# Revit family: LL-Double Angle
name_source: partatom
category: Structural Framing
revit_build: Autodesk Revit Architecture 2012 (Build: 20110210_1515)
units: mm (PartAtom-declared; Revit-internal decimal feet)

## types (597) — shared parameters
Assembly Code = B10

## per-type parameters (varying)
| type | A | Legs | Space | W | b | d | t | y |
| 2L8X8X1-1/8 | 33.6 in² | Equal | 0' - 0" | 114 | 0' - 8" | 0' - 8" | 0' - 1 1/8" | 0' - 2 3/8" |
| 2L8X8X1-1/8X3/8 | 33.6 in² | Equal | 0' - 0 3/8" | 114 | 0' - 8" | 0' - 8" | 0' - 1 1/8" | 0' - 2 3/8" |
| 2L8X8X1-1/8X3/4 | 33.6 in² | Equal | 0' - 0 3/4" | 114 | 0' - 8" | 0' - 8" | 0' - 1 1/8" | 0' - 2 3/8" |
| 2L8X8X1 | 30.2 in² | Equal | 0' - 0" | 103 | 0' - 8" | 0' - 8" | 0' - 1" | 0' - 2 3/8" |
| 2L8X8X1X3/8 | 30.2 in² | Equal | 0' - 0 3/8" | 103 | 0' - 8" | 0' - 8" | 0' - 1" | 0' - 2 3/8" |
| 2L8X8X1X3/4 | 30.2 in² | Equal | 0' - 0 3/4" | 103 | 0' - 8" | 0' - 8" | 0' - 1" | 0' - 2 3/8" |
| 2L8X8X7/8 | 26.6 in² | Equal | 0' - 0" | 90.6 | 0' - 8" | 0' - 8" | 0' - 0 7/8" | 0' - 2 5/16" |
| 2L8X8X7/8X3/8 | 26.6 in² | Equal | 0' - 0 3/8" | 90.6 | 0' - 8" | 0' - 8" | 0' - 0 7/8" | 0' - 2 5/16" |
| 2L8X8X7/8X3/4 | 26.6 in² | Equal | 0' - 0 3/4" | 90.6 | 0' - 8" | 0' - 8" | 0' - 0 7/8" | 0' - 2 5/16" |
| 2L8X8X3/4 | 23 in² | Equal | 0' - 0" | 78.4 | 0' - 8" | 0' - 8" | 0' - 0 3/4" | 0' - 2 1/4" |
| 2L8X8X3/4X3/8 | 23 in² | Equal | 0' - 0 3/8" | 78.4 | 0' - 8" | 0' - 8" | 0' - 0 3/4" | 0' - 2 1/4" |
| 2L8X8X3/4X3/4 | 23 in² | Equal | 0' - 0 3/4" | 78.4 | 0' - 8" | 0' - 8" | 0' - 0 3/4" | 0' - 2 1/4" |
| 2L8X8X5/8 | 19.4 in² | Equal | 0' - 0" | 66 | 0' - 8" | 0' - 8" | 0' - 0 5/8" | 0' - 2 3/16" |
| 2L8X8X5/8X3/8 | 19.4 in² | Equal | 0' - 0 3/8" | 66 | 0' - 8" | 0' - 8" | 0' - 0 5/8" | 0' - 2 3/16" |
| 2L8X8X5/8X3/4 | 19.4 in² | Equal | 0' - 0 3/4" | 66 | 0' - 8" | 0' - 8" | 0' - 0 5/8" | 0' - 2 3/16" |
| 2L8X8X9/16 | 17.5 in² | Equal | 0' - 0" | 59.7 | 0' - 8" | 0' - 8" | 0' - 0 9/16" | 0' - 2 3/16" |
| 2L8X8X9/16X3/8 | 17.5 in² | Equal | 0' - 0 3/8" | 59.7 | 0' - 8" | 0' - 8" | 0' - 0 9/16" | 0' - 2 3/16" |
| 2L8X8X9/16X3/4 | 17.5 in² | Equal | 0' - 0 3/4" | 59.7 | 0' - 8" | 0' - 8" | 0' - 0 9/16" | 0' - 2 3/16" |
| 2L8X8X1/2 | 15.7 in² | Equal | 0' - 0" | 53.3 | 0' - 8" | 0' - 8" | 0' - 0 1/2" | 0' - 2 3/16" |
| 2L8X8X1/2X3/8 | 15.7 in² | Equal | 0' - 0 3/8" | 53.3 | 0' - 8" | 0' - 8" | 0' - 0 1/2" | 0' - 2 3/16" |
| 2L8X8X1/2X3/4 | 15.7 in² | Equal | 0' - 0 3/4" | 53.3 | 0' - 8" | 0' - 8" | 0' - 0 1/2" | 0' - 2 3/16" |
| 2L6X6X1 | 22 in² | Equal | 0' - 0" | 75 | 0' - 6" | 0' - 6" | 0' - 1" | 0' - 1 7/8" |
| 2L6X6X1X3/8 | 22 in² | Equal | 0' - 0 3/8" | 75 | 0' - 6" | 0' - 6" | 0' - 1" | 0' - 1 7/8" |
| 2L6X6X1X3/4 | 22 in² | Equal | 0' - 0 3/4" | 75 | 0' - 6" | 0' - 6" | 0' - 1" | 0' - 1 7/8" |
| 2L6X6X7/8 | 19.5 in² | Equal | 0' - 0" | 66.4 | 0' - 6" | 0' - 6" | 0' - 0 7/8" | 0' - 1 13/16" |
| 2L6X6X7/8X3/8 | 19.5 in² | Equal | 0' - 0 3/8" | 66.4 | 0' - 6" | 0' - 6" | 0' - 0 7/8" | 0' - 1 13/16" |
| 2L6X6X7/8X3/4 | 19.5 in² | Equal | 0' - 0 3/4" | 66.4 | 0' - 6" | 0' - 6" | 0' - 0 7/8" | 0' - 1 13/16" |
| 2L6X6X3/4 | 16.9 in² | Equal | 0' - 0" | 57.6 | 0' - 6" | 0' - 6" | 0' - 0 3/4" | 0' - 1 3/4" |
| 2L6X6X3/4X3/8 | 16.9 in² | Equal | 0' - 0 3/8" | 57.6 | 0' - 6" | 0' - 6" | 0' - 0 3/4" | 0' - 1 3/4" |
| 2L6X6X3/4X3/4 | 16.9 in² | Equal | 0' - 0 3/4" | 57.6 | 0' - 6" | 0' - 6" | 0' - 0 3/4" | 0' - 1 3/4" |
| 2L6X6X5/8 | 14.3 in² | Equal | 0' - 0" | 48.5 | 0' - 6" | 0' - 6" | 0' - 0 5/8" | 0' - 1 3/4" |
| 2L6X6X5/8X3/8 | 14.3 in² | Equal | 0' - 0 3/8" | 48.5 | 0' - 6" | 0' - 6" | 0' - 0 5/8" | 0' - 1 3/4" |
| 2L6X6X5/8X3/4 | 14.3 in² | Equal | 0' - 0 3/4" | 48.5 | 0' - 6" | 0' - 6" | 0' - 0 5/8" | 0' - 1 3/4" |
| 2L6X6X9/16 | 12.9 in² | Equal | 0' - 0" | 43.9 | 0' - 6" | 0' - 6" | 0' - 0 9/16" | 0' - 1 11/16" |
| 2L6X6X9/16X3/8 | 12.9 in² | Equal | 0' - 0 3/8" | 43.9 | 0' - 6" | 0' - 6" | 0' - 0 9/16" | 0' - 1 11/16" |
| 2L6X6X9/16X3/4 | 12.9 in² | Equal | 0' - 0 3/4" | 43.9 | 0' - 6" | 0' - 6" | 0' - 0 9/16" | 0' - 1 11/16" |
| 2L6X6X1/2 | 11.5 in² | Equal | 0' - 0" | 39.3 | 0' - 6" | 0' - 6" | 0' - 0 1/2" | 0' - 1 11/16" |
| 2L6X6X1/2X3/8 | 11.5 in² | Equal | 0' - 0 3/8" | 39.3 | 0' - 6" | 0' - 6" | 0' - 0 1/2" | 0' - 1 11/16" |
| 2L6X6X1/2X3/4 | 11.5 in² | Equal | 0' - 0 3/4" | 39.3 | 0' - 6" | 0' - 6" | 0' - 0 1/2" | 0' - 1 11/16" |
| 2L6X6X7/16 | 10.2 in² | Equal | 0' - 0" | 34.6 | 0' - 6" | 0' - 6" | 0' - 0 7/16" | 0' - 1 5/8" |
| 2L6X6X7/16X3/8 | 10.2 in² | Equal | 0' - 0 3/8" | 34.6 | 0' - 6" | 0' - 6" | 0' - 0 7/16" | 0' - 1 5/8" |
| 2L6X6X7/16X3/4 | 10.2 in² | Equal | 0' - 0 3/4" | 34.6 | 0' - 6" | 0' - 6" | 0' - 0 7/16" | 0' - 1 5/8" |
| 2L6X6X3/8 | 8.76 in² | Equal | 0' - 0" | 29.8 | 0' - 6" | 0' - 6" | 0' - 0 3/8" | 0' - 1 5/8" |
| 2L6X6X3/8X3/8 | 8.76 in² | Equal | 0' - 0 3/8" | 29.8 | 0' - 6" | 0' - 6" | 0' - 0 3/8" | 0' - 1 5/8" |
| 2L6X6X3/8X3/4 | 8.76 in² | Equal | 0' - 0 3/4" | 29.8 | 0' - 6" | 0' - 6" | 0' - 0 3/8" | 0' - 1 5/8" |
| 2L6X6X5/16 | 7.34 in² | Equal | 0' - 0" | 25 | 0' - 6" | 0' - 6" | 0' - 0 5/16" | 0' - 1 5/8" |
| 2L6X6X5/16X3/8 | 7.34 in² | Equal | 0' - 0 3/8" | 25 | 0' - 6" | 0' - 6" | 0' - 0 5/16" | 0' - 1 5/8" |
| 2L6X6X5/16X3/4 | 7.34 in² | Equal | 0' - 0 3/4" | 25 | 0' - 6" | 0' - 6" | 0' - 0 5/16" | 0' - 1 5/8" |
| 2L5X5X7/8 | 16 in² | Equal | 0' - 0" | 54.6 | 0' - 5" | 0' - 5" | 0' - 0 7/8" | 0' - 1 9/16" |
| 2L5X5X7/8X3/8 | 16 in² | Equal | 0' - 0 3/8" | 54.6 | 0' - 5" | 0' - 5" | 0' - 0 7/8" | 0' - 1 9/16" |
| 2L5X5X7/8X3/4 | 16 in² | Equal | 0' - 0 3/4" | 54.6 | 0' - 5" | 0' - 5" | 0' - 0 7/8" | 0' - 1 9/16" |
| 2L5X5X3/4 | 14 in² | Equal | 0' - 0" | 47.5 | 0' - 5" | 0' - 5" | 0' - 0 3/4" | 0' - 1 1/2" |
| 2L5X5X3/4X3/8 | 14 in² | Equal | 0' - 0 3/8" | 47.5 | 0' - 5" | 0' - 5" | 0' - 0 3/4" | 0' - 1 1/2" |
| 2L5X5X3/4X3/4 | 14 in² | Equal | 0' - 0 3/4" | 47.5 | 0' - 5" | 0' - 5" | 0' - 0 3/4" | 0' - 1 1/2" |
| 2L5X5X5/8 | 11.8 in² | Equal | 0' - 0" | 40.1 | 0' - 5" | 0' - 5" | 0' - 0 5/8" | 0' - 1 1/2" |
| 2L5X5X5/8X3/8 | 11.8 in² | Equal | 0' - 0 3/8" | 40.1 | 0' - 5" | 0' - 5" | 0' - 0 5/8" | 0' - 1 1/2" |
| 2L5X5X5/8X3/4 | 11.8 in² | Equal | 0' - 0 3/4" | 40.1 | 0' - 5" | 0' - 5" | 0' - 0 5/8" | 0' - 1 1/2" |
| 2L5X5X1/2 | 9.58 in² | Equal | 0' - 0" | 32.6 | 0' - 5" | 0' - 5" | 0' - 0 1/2" | 0' - 1 7/16" |
| 2L5X5X1/2X3/8 | 9.58 in² | Equal | 0' - 0 3/8" | 32.6 | 0' - 5" | 0' - 5" | 0' - 0 1/2" | 0' - 1 7/16" |
| 2L5X5X1/2X3/4 | 9.58 in² | Equal | 0' - 0 3/4" | 32.6 | 0' - 5" | 0' - 5" | 0' - 0 1/2" | 0' - 1 7/16" |
| 2L5X5X7/16 | 8.44 in² | Equal | 0' - 0" | 28.7 | 0' - 5" | 0' - 5" | 0' - 0 7/16" | 0' - 1 3/8" |
| 2L5X5X7/16X3/8 | 8.44 in² | Equal | 0' - 0 3/8" | 28.7 | 0' - 5" | 0' - 5" | 0' - 0 7/16" | 0' - 1 3/8" |
| 2L5X5X7/16X3/4 | 8.44 in² | Equal | 0' - 0 3/4" | 28.7 | 0' - 5" | 0' - 5" | 0' - 0 7/16" | 0' - 1 3/8" |
| 2L5X5X3/8 | 7.3 in² | Equal | 0' - 0" | 24.8 | 0' - 5" | 0' - 5" | 0' - 0 3/8" | 0' - 1 3/8" |
| 2L5X5X3/8X3/8 | 7.3 in² | Equal | 0' - 0 3/8" | 24.8 | 0' - 5" | 0' - 5" | 0' - 0 3/8" | 0' - 1 3/8" |
| 2L5X5X3/8X3/4 | 7.3 in² | Equal | 0' - 0 3/4" | 24.8 | 0' - 5" | 0' - 5" | 0' - 0 3/8" | 0' - 1 3/8" |
| 2L5X5X5/16 | 6.13 in² | Equal | 0' - 0" | 20.9 | 0' - 5" | 0' - 5" | 0' - 0 5/16" | 0' - 1 3/8" |
| 2L5X5X5/16X3/8 | 6.13 in² | Equal | 0' - 0 3/8" | 20.9 | 0' - 5" | 0' - 5" | 0' - 0 5/16" | 0' - 1 3/8" |
| 2L5X5X5/16X3/4 | 6.13 in² | Equal | 0' - 0 3/4" | 20.9 | 0' - 5" | 0' - 5" | 0' - 0 5/16" | 0' - 1 3/8" |
| 2L4X4X3/4 | 10.9 in² | Equal | 0' - 0" | 37 | 0' - 4" | 0' - 4" | 0' - 0 3/4" | 0' - 1 1/4" |
| 2L4X4X3/4X3/8 | 10.9 in² | Equal | 0' - 0 3/8" | 37 | 0' - 4" | 0' - 4" | 0' - 0 3/4" | 0' - 1 1/4" |
| 2L4X4X3/4X3/4 | 10.9 in² | Equal | 0' - 0 3/4" | 37 | 0' - 4" | 0' - 4" | 0' - 0 3/4" | 0' - 1 1/4" |
| 2L4X4X5/8 | 9.21 in² | Equal | 0' - 0" | 31.3 | 0' - 4" | 0' - 4" | 0' - 0 5/8" | 0' - 1 1/4" |
| 2L4X4X5/8X3/8 | 9.21 in² | Equal | 0' - 0 3/8" | 31.3 | 0' - 4" | 0' - 4" | 0' - 0 5/8" | 0' - 1 1/4" |
| 2L4X4X5/8X3/4 | 9.21 in² | Equal | 0' - 0 3/4" | 31.3 | 0' - 4" | 0' - 4" | 0' - 0 5/8" | 0' - 1 1/4" |
| 2L4X4X1/2 | 7.49 in² | Equal | 0' - 0" | 25.5 | 0' - 4" | 0' - 4" | 0' - 0 1/2" | 0' - 1 3/16" |
| 2L4X4X1/2X3/8 | 7.49 in² | Equal | 0' - 0 3/8" | 25.5 | 0' - 4" | 0' - 4" | 0' - 0 1/2" | 0' - 1 3/16" |
| 2L4X4X1/2X3/4 | 7.49 in² | Equal | 0' - 0 3/4" | 25.5 | 0' - 4" | 0' - 4" | 0' - 0 1/2" | 0' - 1 3/16" |
| 2L4X4X7/16 | 6.61 in² | Equal | 0' - 0" | 22.5 | 0' - 4" | 0' - 4" | 0' - 0 7/16" | 0' - 1 1/8" |
| 2L4X4X7/16X3/8 | 6.61 in² | Equal | 0' - 0 3/8" | 22.5 | 0' - 4" | 0' - 4" | 0' - 0 7/16" | 0' - 1 1/8" |
| 2L4X4X7/16X3/4 | 6.61 in² | Equal | 0' - 0 3/4" | 22.5 | 0' - 4" | 0' - 4" | 0' - 0 7/16" | 0' - 1 1/8" |
| 2L4X4X3/8 | 5.71 in² | Equal | 0' - 0" | 19.4 | 0' - 4" | 0' - 4" | 0' - 0 3/8" | 0' - 1 1/8" |
| 2L4X4X3/8X3/8 | 5.71 in² | Equal | 0' - 0 3/8" | 19.4 | 0' - 4" | 0' - 4" | 0' - 0 3/8" | 0' - 1 1/8" |
| 2L4X4X3/8X3/4 | 5.71 in² | Equal | 0' - 0 3/4" | 19.4 | 0' - 4" | 0' - 4" | 0' - 0 3/8" | 0' - 1 1/8" |
| 2L4X4X5/16 | 4.8 in² | Equal | 0' - 0" | 16.3 | 0' - 4" | 0' - 4" | 0' - 0 5/16" | 0' - 1 1/8" |
| 2L4X4X5/16X3/8 | 4.8 in² | Equal | 0' - 0 3/8" | 16.3 | 0' - 4" | 0' - 4" | 0' - 0 5/16" | 0' - 1 1/8" |
| 2L4X4X5/16X3/4 | 4.8 in² | Equal | 0' - 0 3/4" | 16.3 | 0' - 4" | 0' - 4" | 0' - 0 5/16" | 0' - 1 1/8" |
| 2L4X4X1/4 | 3.87 in² | Equal | 0' - 0" | 13.2 | 0' - 4" | 0' - 4" | 0' - 0 1/4" | 0' - 1 1/16" |
| 2L4X4X1/4X3/8 | 3.87 in² | Equal | 0' - 0 3/8" | 13.2 | 0' - 4" | 0' - 4" | 0' - 0 1/4" | 0' - 1 1/16" |
| 2L4X4X1/4X3/4 | 3.87 in² | Equal | 0' - 0 3/4" | 13.2 | 0' - 4" | 0' - 4" | 0' - 0 1/4" | 0' - 1 1/16" |
| 2L3-1/2X3-1/2X1/2 | 6.53 in² | Equal | 0' - 0" | 22.2 | 0' - 3 1/2" | 0' - 3 1/2" | 0' - 0 1/2" | 0' - 1 1/16" |
| 2L3-1/2X3-1/2X1/2X3/8 | 6.53 in² | Equal | 0' - 0 3/8" | 22.2 | 0' - 3 1/2" | 0' - 3 1/2" | 0' - 0 1/2" | 0' - 1 1/16" |
| 2L3-1/2X3-1/2X1/2X3/4 | 6.53 in² | Equal | 0' - 0 3/4" | 22.2 | 0' - 3 1/2" | 0' - 3 1/2" | 0' - 0 1/2" | 0' - 1 1/16" |
| 2L3-1/2X3-1/2X7/16 | 5.77 in² | Equal | 0' - 0" | 19.6 | 0' - 3 1/2" | 0' - 3 1/2" | 0' - 0 7/16" | 0' - 1" |
| 2L3-1/2X3-1/2X7/16X3/8 | 5.77 in² | Equal | 0' - 0 3/8" | 19.6 | 0' - 3 1/2" | 0' - 3 1/2" | 0' - 0 7/16" | 0' - 1" |
| 2L3-1/2X3-1/2X7/16X3/4 | 5.77 in² | Equal | 0' - 0 3/4" | 19.6 | 0' - 3 1/2" | 0' - 3 1/2" | 0' - 0 7/16" | 0' - 1" |
| 2L3-1/2X3-1/2X3/8 | 5 in² | Equal | 0' - 0" | 17 | 0' - 3 1/2" | 0' - 3 1/2" | 0' - 0 3/8" | 0' - 1" |
| 2L3-1/2X3-1/2X3/8X3/8 | 5 in² | Equal | 0' - 0 3/8" | 17 | 0' - 3 1/2" | 0' - 3 1/2" | 0' - 0 3/8" | 0' - 1" |
| 2L3-1/2X3-1/2X3/8X3/4 | 5 in² | Equal | 0' - 0 3/4" | 17 | 0' - 3 1/2" | 0' - 3 1/2" | 0' - 0 3/8" | 0' - 1" |
| 2L3-1/2X3-1/2X5/16 | 4.21 in² | Equal | 0' - 0" | 14.3 | 0' - 3 1/2" | 0' - 3 1/2" | 0' - 0 5/16" | 0' - 1" |
| 2L3-1/2X3-1/2X5/16X3/8 | 4.21 in² | Equal | 0' - 0 3/8" | 14.3 | 0' - 3 1/2" | 0' - 3 1/2" | 0' - 0 5/16" | 0' - 1" |
| 2L3-1/2X3-1/2X5/16X3/4 | 4.21 in² | Equal | 0' - 0 3/4" | 14.3 | 0' - 3 1/2" | 0' - 3 1/2" | 0' - 0 5/16" | 0' - 1" |
| 2L3-1/2X3-1/2X1/4 | 3.41 in² | Equal | 0' - 0" | 11.6 | 0' - 3 1/2" | 0' - 3 1/2" | 0' - 0 1/4" | 0' - 0 15/16" |
| 2L3-1/2X3-1/2X1/4X3/8 | 3.41 in² | Equal | 0' - 0 3/8" | 11.6 | 0' - 3 1/2" | 0' - 3 1/2" | 0' - 0 1/4" | 0' - 0 15/16" |
| 2L3-1/2X3-1/2X1/4X3/4 | 3.41 in² | Equal | 0' - 0 3/4" | 11.6 | 0' - 3 1/2" | 0' - 3 1/2" | 0' - 0 1/4" | 0' - 0 15/16" |
| 2L3X3X1/2 | 5.5 in² | Equal | 0' - 0" | 18.7 | 0' - 3" | 0' - 3" | 0' - 0 1/2" | 0' - 0 15/16" |
| 2L3X3X1/2X3/8 | 5.5 in² | Equal | 0' - 0 3/8" | 18.7 | 0' - 3" | 0' - 3" | 0' - 0 1/2" | 0' - 0 15/16" |
| 2L3X3X1/2X3/4 | 5.5 in² | Equal | 0' - 0 3/4" | 18.7 | 0' - 3" | 0' - 3" | 0' - 0 1/2" | 0' - 0 15/16" |
| 2L3X3X7/16 | 4.86 in² | Equal | 0' - 0" | 16.6 | 0' - 3" | 0' - 3" | 0' - 0 7/16" | 0' - 0 15/16" |
| 2L3X3X7/16X3/8 | 4.86 in² | Equal | 0' - 0 3/8" | 16.6 | 0' - 3" | 0' - 3" | 0' - 0 7/16" | 0' - 0 15/16" |
| 2L3X3X7/16X3/4 | 4.86 in² | Equal | 0' - 0 3/4" | 16.6 | 0' - 3" | 0' - 3" | 0' - 0 7/16" | 0' - 0 15/16" |
| 2L3X3X3/8 | 4.22 in² | Equal | 0' - 0" | 14.3 | 0' - 3" | 0' - 3" | 0' - 0 3/8" | 0' - 0 7/8" |
| 2L3X3X3/8X3/8 | 4.22 in² | Equal | 0' - 0 3/8" | 14.3 | 0' - 3" | 0' - 3" | 0' - 0 3/8" | 0' - 0 7/8" |
| 2L3X3X3/8X3/4 | 4.22 in² | Equal | 0' - 0 3/4" | 14.3 | 0' - 3" | 0' - 3" | 0' - 0 3/8" | 0' - 0 7/8" |
| 2L3X3X5/16 | 3.55 in² | Equal | 0' - 0" | 12.1 | 0' - 3" | 0' - 3" | 0' - 0 5/16" | 0' - 0 7/8" |
| 2L3X3X5/16X3/8 | 3.55 in² | Equal | 0' - 0 3/8" | 12.1 | 0' - 3" | 0' - 3" | 0' - 0 5/16" | 0' - 0 7/8" |
| 2L3X3X5/16X3/4 | 3.55 in² | Equal | 0' - 0 3/4" | 12.1 | 0' - 3" | 0' - 3" | 0' - 0 5/16" | 0' - 0 7/8" |
| 2L3X3X1/4 | 2.87 in² | Equal | 0' - 0" | 9.77 | 0' - 3" | 0' - 3" | 0' - 0 1/4" | 0' - 0 13/16" |
| 2L3X3X1/4X3/8 | 2.87 in² | Equal | 0' - 0 3/8" | 9.77 | 0' - 3" | 0' - 3" | 0' - 0 1/4" | 0' - 0 13/16" |
| 2L3X3X1/4X3/4 | 2.87 in² | Equal | 0' - 0 3/4" | 9.77 | 0' - 3" | 0' - 3" | 0' - 0 1/4" | 0' - 0 13/16" |
| 2L3X3X3/16 | 2.18 in² | Equal | 0' - 0" | 7.41 | 0' - 3" | 0' - 3" | 0' - 0 3/16" | 0' - 0 13/16" |
| 2L3X3X3/16X3/8 | 2.18 in² | Equal | 0' - 0 3/8" | 7.41 | 0' - 3" | 0' - 3" | 0' - 0 3/16" | 0' - 0 13/16" |
| 2L3X3X3/16X3/4 | 2.18 in² | Equal | 0' - 0 3/4" | 7.41 | 0' - 3" | 0' - 3" | 0' - 0 3/16" | 0' - 0 13/16" |
| 2L2-1/2X2-1/2X1/2 | 4.5 in² | Equal | 0' - 0" | 15.3 | 0' - 2 1/2" | 0' - 2 1/2" | 0' - 0 1/2" | 0' - 0 13/16" |
| 2L2-1/2X2-1/2X1/2X3/8 | 4.5 in² | Equal | 0' - 0 3/8" | 15.3 | 0' - 2 1/2" | 0' - 2 1/2" | 0' - 0 1/2" | 0' - 0 13/16" |
| 2L2-1/2X2-1/2X1/2X3/4 | 4.5 in² | Equal | 0' - 0 3/4" | 15.3 | 0' - 2 1/2" | 0' - 2 1/2" | 0' - 0 1/2" | 0' - 0 13/16" |
| 2L2-1/2X2-1/2X3/8 | 3.47 in² | Equal | 0' - 0" | 11.8 | 0' - 2 1/2" | 0' - 2 1/2" | 0' - 0 3/8" | 0' - 0 3/4" |
| 2L2-1/2X2-1/2X3/8X3/8 | 3.47 in² | Equal | 0' - 0 3/8" | 11.8 | 0' - 2 1/2" | 0' - 2 1/2" | 0' - 0 3/8" | 0' - 0 3/4" |
| 2L2-1/2X2-1/2X3/8X3/4 | 3.47 in² | Equal | 0' - 0 3/4" | 11.8 | 0' - 2 1/2" | 0' - 2 1/2" | 0' - 0 3/8" | 0' - 0 3/4" |
| 2L2-1/2X2-1/2X5/16 | 2.93 in² | Equal | 0' - 0" | 10 | 0' - 2 1/2" | 0' - 2 1/2" | 0' - 0 5/16" | 0' - 0 3/4" |
| 2L2-1/2X2-1/2X5/16X3/8 | 2.93 in² | Equal | 0' - 0 3/8" | 10 | 0' - 2 1/2" | 0' - 2 1/2" | 0' - 0 5/16" | 0' - 0 3/4" |
| 2L2-1/2X2-1/2X5/16X3/4 | 2.93 in² | Equal | 0' - 0 3/4" | 10 | 0' - 2 1/2" | 0' - 2 1/2" | 0' - 0 5/16" | 0' - 0 3/4" |
| 2L2-1/2X2-1/2X1/4 | 2.37 in² | Equal | 0' - 0" | 8.07 | 0' - 2 1/2" | 0' - 2 1/2" | 0' - 0 1/4" | 0' - 0 11/16" |
| 2L2-1/2X2-1/2X1/4X3/8 | 2.37 in² | Equal | 0' - 0 3/8" | 8.07 | 0' - 2 1/2" | 0' - 2 1/2" | 0' - 0 1/4" | 0' - 0 11/16" |
| 2L2-1/2X2-1/2X1/4X3/4 | 2.37 in² | Equal | 0' - 0 3/4" | 8.07 | 0' - 2 1/2" | 0' - 2 1/2" | 0' - 0 1/4" | 0' - 0 11/16" |
| 2L2-1/2X2-1/2X3/16 | 1.8 in² | Equal | 0' - 0" | 6.13 | 0' - 2 1/2" | 0' - 2 1/2" | 0' - 0 3/16" | 0' - 0 11/16" |
| 2L2-1/2X2-1/2X3/16X3/8 | 1.8 in² | Equal | 0' - 0 3/8" | 6.13 | 0' - 2 1/2" | 0' - 2 1/2" | 0' - 0 3/16" | 0' - 0 11/16" |
| 2L2-1/2X2-1/2X3/16X3/4 | 1.8 in² | Equal | 0' - 0 3/4" | 6.13 | 0' - 2 1/2" | 0' - 2 1/2" | 0' - 0 3/16" | 0' - 0 11/16" |
| 2L2X2X3/8 | 2.73 in² | Equal | 0' - 0" | 9.3 | 0' - 2" | 0' - 2" | 0' - 0 3/8" | 0' - 0 5/8" |
| 2L2X2X3/8X3/8 | 2.73 in² | Equal | 0' - 0 3/8" | 9.3 | 0' - 2" | 0' - 2" | 0' - 0 3/8" | 0' - 0 5/8" |
| 2L2X2X3/8X3/4 | 2.73 in² | Equal | 0' - 0 3/4" | 9.3 | 0' - 2" | 0' - 2" | 0' - 0 3/8" | 0' - 0 5/8" |
| 2L2X2X5/16 | 2.32 in² | Equal | 0' - 0" | 7.89 | 0' - 2" | 0' - 2" | 0' - 0 5/16" | 0' - 0 5/8" |
| 2L2X2X5/16X3/8 | 2.32 in² | Equal | 0' - 0 3/8" | 7.89 | 0' - 2" | 0' - 2" | 0' - 0 5/16" | 0' - 0 5/8" |
| 2L2X2X5/16X3/4 | 2.32 in² | Equal | 0' - 0 3/4" | 7.89 | 0' - 2" | 0' - 2" | 0' - 0 5/16" | 0' - 0 5/8" |
| 2L2X2X1/4 | 1.89 in² | Equal | 0' - 0" | 6.43 | 0' - 2" | 0' - 2" | 0' - 0 1/4" | 0' - 0 9/16" |
| 2L2X2X1/4X3/8 | 1.89 in² | Equal | 0' - 0 3/8" | 6.43 | 0' - 2" | 0' - 2" | 0' - 0 1/4" | 0' - 0 9/16" |
| 2L2X2X1/4X3/4 | 1.89 in² | Equal | 0' - 0 3/4" | 6.43 | 0' - 2" | 0' - 2" | 0' - 0 1/4" | 0' - 0 9/16" |
| 2L2X2X3/16 | 1.44 in² | Equal | 0' - 0" | 4.91 | 0' - 2" | 0' - 2" | 0' - 0 3/16" | 0' - 0 9/16" |
| 2L2X2X3/16X3/8 | 1.44 in² | Equal | 0' - 0 3/8" | 4.91 | 0' - 2" | 0' - 2" | 0' - 0 3/16" | 0' - 0 9/16" |
| 2L2X2X3/16X3/4 | 1.44 in² | Equal | 0' - 0 3/4" | 4.91 | 0' - 2" | 0' - 2" | 0' - 0 3/16" | 0' - 0 9/16" |
| 2L2X2X1/8 | 0.98 in² | Equal | 0' - 0" | 3.34 | 0' - 2" | 0' - 2" | 0' - 0 1/8" | 0' - 0 9/16" |
| 2L2X2X1/8X3/8 | 0.98 in² | Equal | 0' - 0 3/8" | 3.34 | 0' - 2" | 0' - 2" | 0' - 0 1/8" | 0' - 0 9/16" |
| 2L2X2X1/8X3/4 | 0.98 in² | Equal | 0' - 0 3/4" | 3.34 | 0' - 2" | 0' - 2" | 0' - 0 1/8" | 0' - 0 9/16" |
| 2L8X6X1LLBB | 26.1 in² | LLBB | 0' - 0" | 88.8 | 0' - 6" | 0' - 8" | 0' - 1" | 0' - 2 5/8" |
| 2L8X6X1X3/8LLBB | 26.1 in² | LLBB | 0' - 0 3/8" | 88.8 | 0' - 6" | 0' - 8" | 0' - 1" | 0' - 2 5/8" |
| 2L8X6X1X3/4LLBB | 26.1 in² | LLBB | 0' - 0 3/4" | 88.8 | 0' - 6" | 0' - 8" | 0' - 1" | 0' - 2 5/8" |
| 2L8X6X7/8LLBB | 23.1 in² | LLBB | 0' - 0" | 78.5 | 0' - 6" | 0' - 8" | 0' - 0 7/8" | 0' - 2 5/8" |
| 2L8X6X7/8X3/8LLBB | 23.1 in² | LLBB | 0' - 0 3/8" | 78.5 | 0' - 6" | 0' - 8" | 0' - 0 7/8" | 0' - 2 5/8" |
| 2L8X6X7/8X3/4LLBB | 23.1 in² | LLBB | 0' - 0 3/4" | 78.5 | 0' - 6" | 0' - 8" | 0' - 0 7/8" | 0' - 2 5/8" |
| 2L8X6X3/4LLBB | 20 in² | LLBB | 0' - 0" | 68 | 0' - 6" | 0' - 8" | 0' - 0 3/4" | 0' - 2 9/16" |
| 2L8X6X3/4X3/8LLBB | 20 in² | LLBB | 0' - 0 3/8" | 68 | 0' - 6" | 0' - 8" | 0' - 0 3/4" | 0' - 2 9/16" |
| 2L8X6X3/4X3/4LLBB | 20 in² | LLBB | 0' - 0 3/4" | 68 | 0' - 6" | 0' - 8" | 0' - 0 3/4" | 0' - 2 9/16" |
| 2L8X6X5/8LLBB | 16.8 in² | LLBB | 0' - 0" | 57.3 | 0' - 6" | 0' - 8" | 0' - 0 5/8" | 0' - 2 1/2" |
| 2L8X6X5/8X3/8LLBB | 16.8 in² | LLBB | 0' - 0 3/8" | 57.3 | 0' - 6" | 0' - 8" | 0' - 0 5/8" | 0' - 2 1/2" |
| 2L8X6X5/8X3/4LLBB | 16.8 in² | LLBB | 0' - 0 3/4" | 57.3 | 0' - 6" | 0' - 8" | 0' - 0 5/8" | 0' - 2 1/2" |
| 2L8X6X9/16LLBB | 15.2 in² | LLBB | 0' - 0" | 51.8 | 0' - 6" | 0' - 8" | 0' - 0 9/16" | 0' - 2 1/2" |
| 2L8X6X9/16X3/8LLBB | 15.2 in² | LLBB | 0' - 0 3/8" | 51.8 | 0' - 6" | 0' - 8" | 0' - 0 9/16" | 0' - 2 1/2" |
| 2L8X6X9/16X3/4LLBB | 15.2 in² | LLBB | 0' - 0 3/4" | 51.8 | 0' - 6" | 0' - 8" | 0' - 0 9/16" | 0' - 2 1/2" |
| 2L8X6X1/2LLBB | 13.6 in² | LLBB | 0' - 0" | 46.3 | 0' - 6" | 0' - 8" | 0' - 0 1/2" | 0' - 2 7/16" |
| 2L8X6X1/2X3/8LLBB | 13.6 in² | LLBB | 0' - 0 3/8" | 46.3 | 0' - 6" | 0' - 8" | 0' - 0 1/2" | 0' - 2 7/16" |
| 2L8X6X1/2X3/4LLBB | 13.6 in² | LLBB | 0' - 0 3/4" | 46.3 | 0' - 6" | 0' - 8" | 0' - 0 1/2" | 0' - 2 7/16" |
| 2L8X6X7/16LLBB | 12 in² | LLBB | 0' - 0" | 40.7 | 0' - 6" | 0' - 8" | 0' - 0 7/16" | 0' - 2 7/16" |
| 2L8X6X7/16X3/8LLBB | 12 in² | LLBB | 0' - 0 3/8" | 40.7 | 0' - 6" | 0' - 8" | 0' - 0 7/16" | 0' - 2 7/16" |
| 2L8X6X7/16X3/4LLBB | 12 in² | LLBB | 0' - 0 3/4" | 40.7 | 0' - 6" | 0' - 8" | 0' - 0 7/16" | 0' - 2 7/16" |
| 2L8X4X1LLBB | 22.1 in² | LLBB | 0' - 0" | 75.2 | 0' - 4" | 0' - 8" | 0' - 1" | 0' - 3" |
| 2L8X4X1X3/8LLBB | 22.1 in² | LLBB | 0' - 0 3/8" | 75.2 | 0' - 4" | 0' - 8" | 0' - 1" | 0' - 3" |
| 2L8X4X1X3/4LLBB | 22.1 in² | LLBB | 0' - 0 3/4" | 75.2 | 0' - 4" | 0' - 8" | 0' - 1" | 0' - 3" |
| 2L8X4X7/8LLBB | 19.6 in² | LLBB | 0' - 0" | 66.6 | 0' - 4" | 0' - 8" | 0' - 0 7/8" | 0' - 3" |
| 2L8X4X7/8X3/8LLBB | 19.6 in² | LLBB | 0' - 0 3/8" | 66.6 | 0' - 4" | 0' - 8" | 0' - 0 7/8" | 0' - 3" |
| 2L8X4X7/8X3/4LLBB | 19.6 in² | LLBB | 0' - 0 3/4" | 66.6 | 0' - 4" | 0' - 8" | 0' - 0 7/8" | 0' - 3" |
| 2L8X4X3/4LLBB | 17 in² | LLBB | 0' - 0" | 57.8 | 0' - 4" | 0' - 8" | 0' - 0 3/4" | 0' - 2 15/16" |
| 2L8X4X3/4X3/8LLBB | 17 in² | LLBB | 0' - 0 3/8" | 57.8 | 0' - 4" | 0' - 8" | 0' - 0 3/4" | 0' - 2 15/16" |
| 2L8X4X3/4X3/4LLBB | 17 in² | LLBB | 0' - 0 3/4" | 57.8 | 0' - 4" | 0' - 8" | 0' - 0 3/4" | 0' - 2 15/16" |
| 2L8X4X5/8LLBB | 14.3 in² | LLBB | 0' - 0" | 48.7 | 0' - 4" | 0' - 8" | 0' - 0 5/8" | 0' - 2 7/8" |
| 2L8X4X5/8X3/8LLBB | 14.3 in² | LLBB | 0' - 0 3/8" | 48.7 | 0' - 4" | 0' - 8" | 0' - 0 5/8" | 0' - 2 7/8" |
| 2L8X4X5/8X3/4LLBB | 14.3 in² | LLBB | 0' - 0 3/4" | 48.7 | 0' - 4" | 0' - 8" | 0' - 0 5/8" | 0' - 2 7/8" |
| 2L8X4X9/16LLBB | 13 in² | LLBB | 0' - 0" | 44.1 | 0' - 4" | 0' - 8" | 0' - 0 9/16" | 0' - 2 7/8" |
| 2L8X4X9/16X3/8LLBB | 13 in² | LLBB | 0' - 0 3/8" | 44.1 | 0' - 4" | 0' - 8" | 0' - 0 9/16" | 0' - 2 7/8" |
| 2L8X4X9/16X3/4LLBB | 13 in² | LLBB | 0' - 0 3/4" | 44.1 | 0' - 4" | 0' - 8" | 0' - 0 9/16" | 0' - 2 7/8" |
| 2L8X4X1/2LLBB | 11.6 in² | LLBB | 0' - 0" | 39.5 | 0' - 4" | 0' - 8" | 0' - 0 1/2" | 0' - 2 13/16" |
| 2L8X4X1/2X3/8LLBB | 11.6 in² | LLBB | 0' - 0 3/8" | 39.5 | 0' - 4" | 0' - 8" | 0' - 0 1/2" | 0' - 2 13/16" |
| 2L8X4X1/2X3/4LLBB | 11.6 in² | LLBB | 0' - 0 3/4" | 39.5 | 0' - 4" | 0' - 8" | 0' - 0 1/2" | 0' - 2 13/16" |
| 2L8X4X7/16LLBB | 10.2 in² | LLBB | 0' - 0" | 34.8 | 0' - 4" | 0' - 8" | 0' - 0 7/16" | 0' - 2 13/16" |
| 2L8X4X7/16X3/8LLBB | 10.2 in² | LLBB | 0' - 0 3/8" | 34.8 | 0' - 4" | 0' - 8" | 0' - 0 7/16" | 0' - 2 13/16" |
| 2L8X4X7/16X3/4LLBB | 10.2 in² | LLBB | 0' - 0 3/4" | 34.8 | 0' - 4" | 0' - 8" | 0' - 0 7/16" | 0' - 2 13/16" |
| 2L7X4X3/4LLBB | 15.4 in² | LLBB | 0' - 0" | 52.4 | 0' - 4" | 0' - 7" | 0' - 0 3/4" | 0' - 2 1/2" |
| 2L7X4X3/4X3/8LLBB | 15.4 in² | LLBB | 0' - 0 3/8" | 52.4 | 0' - 4" | 0' - 7" | 0' - 0 3/4" | 0' - 2 1/2" |
| 2L7X4X3/4X3/4LLBB | 15.4 in² | LLBB | 0' - 0 3/4" | 52.4 | 0' - 4" | 0' - 7" | 0' - 0 3/4" | 0' - 2 1/2" |
| 2L7X4X5/8LLBB | 13 in² | LLBB | 0' - 0" | 44.2 | 0' - 4" | 0' - 7" | 0' - 0 5/8" | 0' - 2 7/16" |
| 2L7X4X5/8X3/8LLBB | 13 in² | LLBB | 0' - 0 3/8" | 44.2 | 0' - 4" | 0' - 7" | 0' - 0 5/8" | 0' - 2 7/16" |
| 2L7X4X5/8X3/4LLBB | 13 in² | LLBB | 0' - 0 3/4" | 44.2 | 0' - 4" | 0' - 7" | 0' - 0 5/8" | 0' - 2 7/16" |
| 2L7X4X1/2LLBB | 10.5 in² | LLBB | 0' - 0" | 35.8 | 0' - 4" | 0' - 7" | 0' - 0 1/2" | 0' - 2 3/8" |
| 2L7X4X1/2X3/8LLBB | 10.5 in² | LLBB | 0' - 0 3/8" | 35.8 | 0' - 4" | 0' - 7" | 0' - 0 1/2" | 0' - 2 3/8" |
| 2L7X4X1/2X3/4LLBB | 10.5 in² | LLBB | 0' - 0 3/4" | 35.8 | 0' - 4" | 0' - 7" | 0' - 0 1/2" | 0' - 2 3/8" |
| 2L7X4X7/16LLBB | 9.27 in² | LLBB | 0' - 0" | 31.5 | 0' - 4" | 0' - 7" | 0' - 0 7/16" | 0' - 2 3/8" |
| 2L7X4X7/16X3/8LLBB | 9.27 in² | LLBB | 0' - 0 3/8" | 31.5 | 0' - 4" | 0' - 7" | 0' - 0 7/16" | 0' - 2 3/8" |
| 2L7X4X7/16X3/4LLBB | 9.27 in² | LLBB | 0' - 0 3/4" | 31.5 | 0' - 4" | 0' - 7" | 0' - 0 7/16" | 0' - 2 3/8" |
| 2L7X4X3/8LLBB | 8 in² | LLBB | 0' - 0" | 27.2 | 0' - 4" | 0' - 7" | 0' - 0 3/8" | 0' - 2 3/8" |
| 2L7X4X3/8X3/8LLBB | 8 in² | LLBB | 0' - 0 3/8" | 27.2 | 0' - 4" | 0' - 7" | 0' - 0 3/8" | 0' - 2 3/8" |
| 2L7X4X3/8X3/4LLBB | 8 in² | LLBB | 0' - 0 3/4" | 27.2 | 0' - 4" | 0' - 7" | 0' - 0 3/8" | 0' - 2 3/8" |
| 2L6X4X7/8LLBB | 16 in² | LLBB | 0' - 0" | 54.3 | 0' - 4" | 0' - 6" | 0' - 0 7/8" | 0' - 2 1/8" |
| 2L6X4X7/8X3/8LLBB | 16 in² | LLBB | 0' - 0 3/8" | 54.3 | 0' - 4" | 0' - 6" | 0' - 0 7/8" | 0' - 2 1/8" |
| 2L6X4X7/8X3/4LLBB | 16 in² | LLBB | 0' - 0 3/4" | 54.3 | 0' - 4" | 0' - 6" | 0' - 0 7/8" | 0' - 2 1/8" |
| 2L6X4X3/4LLBB | 13.9 in² | LLBB | 0' - 0" | 47.2 | 0' - 4" | 0' - 6" | 0' - 0 3/4" | 0' - 2 1/16" |
| 2L6X4X3/4X3/8LLBB | 13.9 in² | LLBB | 0' - 0 3/8" | 47.2 | 0' - 4" | 0' - 6" | 0' - 0 3/4" | 0' - 2 1/16" |
| 2L6X4X3/4X3/4LLBB | 13.9 in² | LLBB | 0' - 0 3/4" | 47.2 | 0' - 4" | 0' - 6" | 0' - 0 3/4" | 0' - 2 1/16" |
| 2L6X4X5/8LLBB | 11.7 in² | LLBB | 0' - 0" | 39.9 | 0' - 4" | 0' - 6" | 0' - 0 5/8" | 0' - 2" |
| 2L6X4X5/8X3/8LLBB | 11.7 in² | LLBB | 0' - 0 3/8" | 39.9 | 0' - 4" | 0' - 6" | 0' - 0 5/8" | 0' - 2" |
| 2L6X4X5/8X3/4LLBB | 11.7 in² | LLBB | 0' - 0 3/4" | 39.9 | 0' - 4" | 0' - 6" | 0' - 0 5/8" | 0' - 2" |
| 2L6X4X9/16LLBB | 10.6 in² | LLBB | 0' - 0" | 36.1 | 0' - 4" | 0' - 6" | 0' - 0 9/16" | 0' - 2" |
| 2L6X4X9/16X3/8LLBB | 10.6 in² | LLBB | 0' - 0 3/8" | 36.1 | 0' - 4" | 0' - 6" | 0' - 0 9/16" | 0' - 2" |
| 2L6X4X9/16X3/4LLBB | 10.6 in² | LLBB | 0' - 0 3/4" | 36.1 | 0' - 4" | 0' - 6" | 0' - 0 9/16" | 0' - 2" |
| 2L6X4X1/2LLBB | 9.5 in² | LLBB | 0' - 0" | 32.3 | 0' - 4" | 0' - 6" | 0' - 0 1/2" | 0' - 2" |
| 2L6X4X1/2X3/8LLBB | 9.5 in² | LLBB | 0' - 0 3/8" | 32.3 | 0' - 4" | 0' - 6" | 0' - 0 1/2" | 0' - 2" |
| 2L6X4X1/2X3/4LLBB | 9.5 in² | LLBB | 0' - 0 3/4" | 32.3 | 0' - 4" | 0' - 6" | 0' - 0 1/2" | 0' - 2" |
| 2L6X4X7/16LLBB | 8.36 in² | LLBB | 0' - 0" | 28.5 | 0' - 4" | 0' - 6" | 0' - 0 7/16" | 0' - 1 15/16" |
| 2L6X4X7/16X3/8LLBB | 8.36 in² | LLBB | 0' - 0 3/8" | 28.5 | 0' - 4" | 0' - 6" | 0' - 0 7/16" | 0' - 1 15/16" |
| 2L6X4X7/16X3/4LLBB | 8.36 in² | LLBB | 0' - 0 3/4" | 28.5 | 0' - 4" | 0' - 6" | 0' - 0 7/16" | 0' - 1 15/16" |
| 2L6X4X3/8LLBB | 7.22 in² | LLBB | 0' - 0" | 24.6 | 0' - 4" | 0' - 6" | 0' - 0 3/8" | 0' - 1 15/16" |
| 2L6X4X3/8X3/8LLBB | 7.22 in² | LLBB | 0' - 0 3/8" | 24.6 | 0' - 4" | 0' - 6" | 0' - 0 3/8" | 0' - 1 15/16" |
| 2L6X4X3/8X3/4LLBB | 7.22 in² | LLBB | 0' - 0 3/4" | 24.6 | 0' - 4" | 0' - 6" | 0' - 0 3/8" | 0' - 1 15/16" |
| 2L6X4X5/16LLBB | 6.05 in² | LLBB | 0' - 0" | 20.6 | 0' - 4" | 0' - 6" | 0' - 0 5/16" | 0' - 1 7/8" |
| 2L6X4X5/16X3/8LLBB | 6.05 in² | LLBB | 0' - 0 3/8" | 20.6 | 0' - 4" | 0' - 6" | 0' - 0 5/16" | 0' - 1 7/8" |
| 2L6X4X5/16X3/4LLBB | 6.05 in² | LLBB | 0' - 0 3/4" | 20.6 | 0' - 4" | 0' - 6" | 0' - 0 5/16" | 0' - 1 7/8" |
| 2L6X3-1/2X1/2LLBB | 9.04 in² | LLBB | 0' - 0" | 30.7 | 0' - 3 1/2" | 0' - 6" | 0' - 0 1/2" | 0' - 2 1/16" |
| 2L6X3-1/2X1/2X3/8LLBB | 9.04 in² | LLBB | 0' - 0 3/8" | 30.7 | 0' - 3 1/2" | 0' - 6" | 0' - 0 1/2" | 0' - 2 1/16" |
| 2L6X3-1/2X1/2X3/4LLBB | 9.04 in² | LLBB | 0' - 0 3/4" | 30.7 | 0' - 3 1/2" | 0' - 6" | 0' - 0 1/2" | 0' - 2 1/16" |
| 2L6X3-1/2X3/8LLBB | 6.88 in² | LLBB | 0' - 0" | 23.4 | 0' - 3 1/2" | 0' - 6" | 0' - 0 3/8" | 0' - 2" |
| 2L6X3-1/2X3/8X3/8LLBB | 6.88 in² | LLBB | 0' - 0 3/8" | 23.4 | 0' - 3 1/2" | 0' - 6" | 0' - 0 3/8" | 0' - 2" |
| 2L6X3-1/2X3/8X3/4LLBB | 6.88 in² | LLBB | 0' - 0 3/4" | 23.4 | 0' - 3 1/2" | 0' - 6" | 0' - 0 3/8" | 0' - 2" |
| 2L6X3-1/2X5/16LLBB | 5.78 in² | LLBB | 0' - 0" | 19.7 | 0' - 3 1/2" | 0' - 6" | 0' - 0 5/16" | 0' - 2" |
| 2L6X3-1/2X5/16X3/8LLBB | 5.78 in² | LLBB | 0' - 0 3/8" | 19.7 | 0' - 3 1/2" | 0' - 6" | 0' - 0 5/16" | 0' - 2" |
| 2L6X3-1/2X5/16X3/4LLBB | 5.78 in² | LLBB | 0' - 0 3/4" | 19.7 | 0' - 3 1/2" | 0' - 6" | 0' - 0 5/16" | 0' - 2" |
| 2L5X3-1/2X3/4LLBB | 11.6 in² | LLBB | 0' - 0" | 39.6 | 0' - 3 1/2" | 0' - 5" | 0' - 0 3/4" | 0' - 1 3/4" |
| 2L5X3-1/2X3/4X3/8LLBB | 11.6 in² | LLBB | 0' - 0 3/8" | 39.6 | 0' - 3 1/2" | 0' - 5" | 0' - 0 3/4" | 0' - 1 3/4" |
| 2L5X3-1/2X3/4X3/4LLBB | 11.6 in² | LLBB | 0' - 0 3/4" | 39.6 | 0' - 3 1/2" | 0' - 5" | 0' - 0 3/4" | 0' - 1 3/4" |
| 2L5X3-1/2X5/8LLBB | 9.85 in² | LLBB | 0' - 0" | 33.5 | 0' - 3 1/2" | 0' - 5" | 0' - 0 5/8" | 0' - 1 11/16" |
| 2L5X3-1/2X5/8X3/8LLBB | 9.85 in² | LLBB | 0' - 0 3/8" | 33.5 | 0' - 3 1/2" | 0' - 5" | 0' - 0 5/8" | 0' - 1 11/16" |
| 2L5X3-1/2X5/8X3/4LLBB | 9.85 in² | LLBB | 0' - 0 3/4" | 33.5 | 0' - 3 1/2" | 0' - 5" | 0' - 0 5/8" | 0' - 1 11/16" |
| 2L5X3-1/2X1/2LLBB | 8.01 in² | LLBB | 0' - 0" | 27.2 | 0' - 3 1/2" | 0' - 5" | 0' - 0 1/2" | 0' - 1 5/8" |
| 2L5X3-1/2X1/2X3/8LLBB | 8.01 in² | LLBB | 0' - 0 3/8" | 27.2 | 0' - 3 1/2" | 0' - 5" | 0' - 0 1/2" | 0' - 1 5/8" |
| 2L5X3-1/2X1/2X3/4LLBB | 8.01 in² | LLBB | 0' - 0 3/4" | 27.2 | 0' - 3 1/2" | 0' - 5" | 0' - 0 1/2" | 0' - 1 5/8" |
| 2L5X3-1/2X3/8LLBB | 6.1 in² | LLBB | 0' - 0" | 20.8 | 0' - 3 1/2" | 0' - 5" | 0' - 0 3/8" | 0' - 1 5/8" |
| 2L5X3-1/2X3/8X3/8LLBB | 6.1 in² | LLBB | 0' - 0 3/8" | 20.8 | 0' - 3 1/2" | 0' - 5" | 0' - 0 3/8" | 0' - 1 5/8" |
| 2L5X3-1/2X3/8X3/4LLBB | 6.1 in² | LLBB | 0' - 0 3/4" | 20.8 | 0' - 3 1/2" | 0' - 5" | 0' - 0 3/8" | 0' - 1 5/8" |
| 2L5X3-1/2X5/16LLBB | 5.12 in² | LLBB | 0' - 0" | 17.4 | 0' - 3 1/2" | 0' - 5" | 0' - 0 5/16" | 0' - 1 9/16" |
| 2L5X3-1/2X5/16X3/8LLBB | 5.12 in² | LLBB | 0' - 0 3/8" | 17.4 | 0' - 3 1/2" | 0' - 5" | 0' - 0 5/16" | 0' - 1 9/16" |
| 2L5X3-1/2X5/16X3/4LLBB | 5.12 in² | LLBB | 0' - 0 3/4" | 17.4 | 0' - 3 1/2" | 0' - 5" | 0' - 0 5/16" | 0' - 1 9/16" |
| 2L5X3-1/2X1/4LLBB | 4.13 in² | LLBB | 0' - 0" | 14.1 | 0' - 3 1/2" | 0' - 5" | 0' - 0 1/4" | 0' - 1 9/16" |
| 2L5X3-1/2X1/4X3/8LLBB | 4.13 in² | LLBB | 0' - 0 3/8" | 14.1 | 0' - 3 1/2" | 0' - 5" | 0' - 0 1/4" | 0' - 1 9/16" |
| 2L5X3-1/2X1/4X3/4LLBB | 4.13 in² | LLBB | 0' - 0 3/4" | 14.1 | 0' - 3 1/2" | 0' - 5" | 0' - 0 1/4" | 0' - 1 9/16" |
| 2L5X3X1/2LLBB | 7.51 in² | LLBB | 0' - 0" | 25.5 | 0' - 3" | 0' - 5" | 0' - 0 1/2" | 0' - 1 3/4" |
| 2L5X3X1/2X3/8LLBB | 7.51 in² | LLBB | 0' - 0 3/8" | 25.5 | 0' - 3" | 0' - 5" | 0' - 0 1/2" | 0' - 1 3/4" |
| 2L5X3X1/2X3/4LLBB | 7.51 in² | LLBB | 0' - 0 3/4" | 25.5 | 0' - 3" | 0' - 5" | 0' - 0 1/2" | 0' - 1 3/4" |
| 2L5X3X7/16LLBB | 6.62 in² | LLBB | 0' - 0" | 22.5 | 0' - 3" | 0' - 5" | 0' - 0 7/16" | 0' - 1 3/4" |
| 2L5X3X7/16X3/8LLBB | 6.62 in² | LLBB | 0' - 0 3/8" | 22.5 | 0' - 3" | 0' - 5" | 0' - 0 7/16" | 0' - 1 3/4" |
| 2L5X3X7/16X3/4LLBB | 6.62 in² | LLBB | 0' - 0 3/4" | 22.5 | 0' - 3" | 0' - 5" | 0' - 0 7/16" | 0' - 1 3/4" |
| 2L5X3X3/8LLBB | 5.73 in² | LLBB | 0' - 0" | 19.5 | 0' - 3" | 0' - 5" | 0' - 0 3/8" | 0' - 1 11/16" |
| 2L5X3X3/8X3/8LLBB | 5.73 in² | LLBB | 0' - 0 3/8" | 19.5 | 0' - 3" | 0' - 5" | 0' - 0 3/8" | 0' - 1 11/16" |
| 2L5X3X3/8X3/4LLBB | 5.73 in² | LLBB | 0' - 0 3/4" | 19.5 | 0' - 3" | 0' - 5" | 0' - 0 3/8" | 0' - 1 11/16" |
| 2L5X3X5/16LLBB | 4.81 in² | LLBB | 0' - 0" | 16.4 | 0' - 3" | 0' - 5" | 0' - 0 5/16" | 0' - 1 11/16" |
| 2L5X3X5/16X3/8LLBB | 4.81 in² | LLBB | 0' - 0 3/8" | 16.4 | 0' - 3" | 0' - 5" | 0' - 0 5/16" | 0' - 1 11/16" |
| 2L5X3X5/16X3/4LLBB | 4.81 in² | LLBB | 0' - 0 3/4" | 16.4 | 0' - 3" | 0' - 5" | 0' - 0 5/16" | 0' - 1 11/16" |
| 2L5X3X1/4LLBB | 3.88 in² | LLBB | 0' - 0" | 13.2 | 0' - 3" | 0' - 5" | 0' - 0 1/4" | 0' - 1 5/8" |
| 2L5X3X1/4X3/8LLBB | 3.88 in² | LLBB | 0' - 0 3/8" | 13.2 | 0' - 3" | 0' - 5" | 0' - 0 1/4" | 0' - 1 5/8" |
| 2L5X3X1/4X3/4LLBB | 3.88 in² | LLBB | 0' - 0 3/4" | 13.2 | 0' - 3" | 0' - 5" | 0' - 0 1/4" | 0' - 1 5/8" |
| 2L4X3-1/2X1/2LLBB | 7.01 in² | LLBB | 0' - 0" | 23.8 | 0' - 3 1/2" | 0' - 4" | 0' - 0 1/2" | 0' - 1 1/4" |
| 2L4X3-1/2X1/2X3/8LLBB | 7.01 in² | LLBB | 0' - 0 3/8" | 23.8 | 0' - 3 1/2" | 0' - 4" | 0' - 0 1/2" | 0' - 1 1/4" |
| 2L4X3-1/2X1/2X3/4LLBB | 7.01 in² | LLBB | 0' - 0 3/4" | 23.8 | 0' - 3 1/2" | 0' - 4" | 0' - 0 1/2" | 0' - 1 1/4" |
| 2L4X3-1/2X3/8LLBB | 5.35 in² | LLBB | 0' - 0" | 18.2 | 0' - 3 1/2" | 0' - 4" | 0' - 0 3/8" | 0' - 1 3/16" |
| 2L4X3-1/2X3/8X3/8LLBB | 5.35 in² | LLBB | 0' - 0 3/8" | 18.2 | 0' - 3 1/2" | 0' - 4" | 0' - 0 3/8" | 0' - 1 3/16" |
| 2L4X3-1/2X3/8X3/4LLBB | 5.35 in² | LLBB | 0' - 0 3/4" | 18.2 | 0' - 3 1/2" | 0' - 4" | 0' - 0 3/8" | 0' - 1 3/16" |
| 2L4X3-1/2X5/16LLBB | 4.5 in² | LLBB | 0' - 0" | 15.3 | 0' - 3 1/2" | 0' - 4" | 0' - 0 5/16" | 0' - 1 3/16" |
| 2L4X3-1/2X5/16X3/8LLBB | 4.5 in² | LLBB | 0' - 0 3/8" | 15.3 | 0' - 3 1/2" | 0' - 4" | 0' - 0 5/16" | 0' - 1 3/16" |
| 2L4X3-1/2X5/16X3/4LLBB | 4.5 in² | LLBB | 0' - 0 3/4" | 15.3 | 0' - 3 1/2" | 0' - 4" | 0' - 0 5/16" | 0' - 1 3/16" |
| 2L4X3-1/2X1/4LLBB | 3.63 in² | LLBB | 0' - 0" | 12.4 | 0' - 3 1/2" | 0' - 4" | 0' - 0 1/4" | 0' - 1 1/8" |
| 2L4X3-1/2X1/4X3/8LLBB | 3.63 in² | LLBB | 0' - 0 3/8" | 12.4 | 0' - 3 1/2" | 0' - 4" | 0' - 0 1/4" | 0' - 1 1/8" |
| 2L4X3-1/2X1/4X3/4LLBB | 3.63 in² | LLBB | 0' - 0 3/4" | 12.4 | 0' - 3 1/2" | 0' - 4" | 0' - 0 1/4" | 0' - 1 1/8" |
| 2L4X3X5/8LLBB | 7.98 in² | LLBB | 0' - 0" | 27.1 | 0' - 3" | 0' - 4" | 0' - 0 5/8" | 0' - 1 3/8" |
| 2L4X3X5/8X3/8LLBB | 7.98 in² | LLBB | 0' - 0 3/8" | 27.1 | 0' - 3" | 0' - 4" | 0' - 0 5/8" | 0' - 1 3/8" |
| 2L4X3X5/8X3/4LLBB | 7.98 in² | LLBB | 0' - 0 3/4" | 27.1 | 0' - 3" | 0' - 4" | 0' - 0 5/8" | 0' - 1 3/8" |
| 2L4X3X1/2LLBB | 6.51 in² | LLBB | 0' - 0" | 22.1 | 0' - 3" | 0' - 4" | 0' - 0 1/2" | 0' - 1 5/16" |
| 2L4X3X1/2X3/8LLBB | 6.51 in² | LLBB | 0' - 0 3/8" | 22.1 | 0' - 3" | 0' - 4" | 0' - 0 1/2" | 0' - 1 5/16" |
| 2L4X3X1/2X3/4LLBB | 6.51 in² | LLBB | 0' - 0 3/4" | 22.1 | 0' - 3" | 0' - 4" | 0' - 0 1/2" | 0' - 1 5/16" |
| 2L4X3X3/8LLBB | 4.98 in² | LLBB | 0' - 0" | 16.9 | 0' - 3" | 0' - 4" | 0' - 0 3/8" | 0' - 1 1/4" |
| 2L4X3X3/8X3/8LLBB | 4.98 in² | LLBB | 0' - 0 3/8" | 16.9 | 0' - 3" | 0' - 4" | 0' - 0 3/8" | 0' - 1 1/4" |
| 2L4X3X3/8X3/4LLBB | 4.98 in² | LLBB | 0' - 0 3/4" | 16.9 | 0' - 3" | 0' - 4" | 0' - 0 3/8" | 0' - 1 1/4" |
| 2L4X3X5/16LLBB | 4.19 in² | LLBB | 0' - 0" | 14.2 | 0' - 3" | 0' - 4" | 0' - 0 5/16" | 0' - 1 1/4" |
| 2L4X3X5/16X3/8LLBB | 4.19 in² | LLBB | 0' - 0 3/8" | 14.2 | 0' - 3" | 0' - 4" | 0' - 0 5/16" | 0' - 1 1/4" |
| 2L4X3X5/16X3/4LLBB | 4.19 in² | LLBB | 0' - 0 3/4" | 14.2 | 0' - 3" | 0' - 4" | 0' - 0 5/16" | 0' - 1 1/4" |
| 2L4X3X1/4LLBB | 3.38 in² | LLBB | 0' - 0" | 11.5 | 0' - 3" | 0' - 4" | 0' - 0 1/4" | 0' - 1 1/4" |
| 2L4X3X1/4X3/8LLBB | 3.38 in² | LLBB | 0' - 0 3/8" | 11.5 | 0' - 3" | 0' - 4" | 0' - 0 1/4" | 0' - 1 1/4" |
| 2L4X3X1/4X3/4LLBB | 3.38 in² | LLBB | 0' - 0 3/4" | 11.5 | 0' - 3" | 0' - 4" | 0' - 0 1/4" | 0' - 1 1/4" |
| 2L3-1/2X3X1/2LLBB | 6.04 in² | LLBB | 0' - 0" | 20.6 | 0' - 3" | 0' - 3 1/2" | 0' - 0 1/2" | 0' - 1 1/8" |
| 2L3-1/2X3X1/2X3/8LLBB | 6.04 in² | LLBB | 0' - 0 3/8" | 20.6 | 0' - 3" | 0' - 3 1/2" | 0' - 0 1/2" | 0' - 1 1/8" |
| 2L3-1/2X3X1/2X3/4LLBB | 6.04 in² | LLBB | 0' - 0 3/4" | 20.6 | 0' - 3" | 0' - 3 1/2" | 0' - 0 1/2" | 0' - 1 1/8" |
| 2L3-1/2X3X7/16LLBB | 5.34 in² | LLBB | 0' - 0" | 18.2 | 0' - 3" | 0' - 3 1/2" | 0' - 0 7/16" | 0' - 1 1/16" |
| 2L3-1/2X3X7/16X3/8LLBB | 5.34 in² | LLBB | 0' - 0 3/8" | 18.2 | 0' - 3" | 0' - 3 1/2" | 0' - 0 7/16" | 0' - 1 1/16" |
| 2L3-1/2X3X7/16X3/4LLBB | 5.34 in² | LLBB | 0' - 0 3/4" | 18.2 | 0' - 3" | 0' - 3 1/2" | 0' - 0 7/16" | 0' - 1 1/16" |
| 2L3-1/2X3X3/8LLBB | 4.63 in² | LLBB | 0' - 0" | 15.8 | 0' - 3" | 0' - 3 1/2" | 0' - 0 3/8" | 0' - 1 1/16" |
| 2L3-1/2X3X3/8X3/8LLBB | 4.63 in² | LLBB | 0' - 0 3/8" | 15.8 | 0' - 3" | 0' - 3 1/2" | 0' - 0 3/8" | 0' - 1 1/16" |
| 2L3-1/2X3X3/8X3/4LLBB | 4.63 in² | LLBB | 0' - 0 3/4" | 15.8 | 0' - 3" | 0' - 3 1/2" | 0' - 0 3/8" | 0' - 1 1/16" |
| 2L3-1/2X3X5/16LLBB | 3.91 in² | LLBB | 0' - 0" | 13.3 | 0' - 3" | 0' - 3 1/2" | 0' - 0 5/16" | 0' - 1 1/16" |
| 2L3-1/2X3X5/16X3/8LLBB | 3.91 in² | LLBB | 0' - 0 3/8" | 13.3 | 0' - 3" | 0' - 3 1/2" | 0' - 0 5/16" | 0' - 1 1/16" |
| 2L3-1/2X3X5/16X3/4LLBB | 3.91 in² | LLBB | 0' - 0 3/4" | 13.3 | 0' - 3" | 0' - 3 1/2" | 0' - 0 5/16" | 0' - 1 1/16" |
| 2L3-1/2X3X1/4LLBB | 3.16 in² | LLBB | 0' - 0" | 10.8 | 0' - 3" | 0' - 3 1/2" | 0' - 0 1/4" | 0' - 1" |
| 2L3-1/2X3X1/4X3/8LLBB | 3.16 in² | LLBB | 0' - 0 3/8" | 10.8 | 0' - 3" | 0' - 3 1/2" | 0' - 0 1/4" | 0' - 1" |
| 2L3-1/2X3X1/4X3/4LLBB | 3.16 in² | LLBB | 0' - 0 3/4" | 10.8 | 0' - 3" | 0' - 3 1/2" | 0' - 0 1/4" | 0' - 1" |
| 2L3-1/2X2-1/2X1/2LLBB | 5.53 in² | LLBB | 0' - 0" | 18.8 | 0' - 2 1/2" | 0' - 3 1/2" | 0' - 0 1/2" | 0' - 1 3/16" |
| 2L3-1/2X2-1/2X1/2X3/8LLBB | 5.53 in² | LLBB | 0' - 0 3/8" | 18.8 | 0' - 2 1/2" | 0' - 3 1/2" | 0' - 0 1/2" | 0' - 1 3/16" |
| 2L3-1/2X2-1/2X1/2X3/4LLBB | 5.53 in² | LLBB | 0' - 0 3/4" | 18.8 | 0' - 2 1/2" | 0' - 3 1/2" | 0' - 0 1/2" | 0' - 1 3/16" |
| 2L3-1/2X2-1/2X3/8LLBB | 4.25 in² | LLBB | 0' - 0" | 14.5 | 0' - 2 1/2" | 0' - 3 1/2" | 0' - 0 3/8" | 0' - 1 1/8" |
| 2L3-1/2X2-1/2X3/8X3/8LLBB | 4.25 in² | LLBB | 0' - 0 3/8" | 14.5 | 0' - 2 1/2" | 0' - 3 1/2" | 0' - 0 3/8" | 0' - 1 1/8" |
| 2L3-1/2X2-1/2X3/8X3/4LLBB | 4.25 in² | LLBB | 0' - 0 3/4" | 14.5 | 0' - 2 1/2" | 0' - 3 1/2" | 0' - 0 3/8" | 0' - 1 1/8" |
| 2L3-1/2X2-1/2X5/16LLBB | 3.58 in² | LLBB | 0' - 0" | 12.2 | 0' - 2 1/2" | 0' - 3 1/2" | 0' - 0 5/16" | 0' - 1 1/8" |
| 2L3-1/2X2-1/2X5/16X3/8LLBB | 3.58 in² | LLBB | 0' - 0 3/8" | 12.2 | 0' - 2 1/2" | 0' - 3 1/2" | 0' - 0 5/16" | 0' - 1 1/8" |
| 2L3-1/2X2-1/2X5/16X3/4LLBB | 3.58 in² | LLBB | 0' - 0 3/4" | 12.2 | 0' - 2 1/2" | 0' - 3 1/2" | 0' - 0 5/16" | 0' - 1 1/8" |
| 2L3-1/2X2-1/2X1/4LLBB | 2.9 in² | LLBB | 0' - 0" | 9.88 | 0' - 2 1/2" | 0' - 3 1/2" | 0' - 0 1/4" | 0' - 1 1/8" |
| 2L3-1/2X2-1/2X1/4X3/8LLBB | 2.9 in² | LLBB | 0' - 0 3/8" | 9.88 | 0' - 2 1/2" | 0' - 3 1/2" | 0' - 0 1/4" | 0' - 1 1/8" |
| 2L3-1/2X2-1/2X1/4X3/4LLBB | 2.9 in² | LLBB | 0' - 0 3/4" | 9.88 | 0' - 2 1/2" | 0' - 3 1/2" | 0' - 0 1/4" | 0' - 1 1/8" |
| 2L3X2-1/2X1/2LLBB | 5.01 in² | LLBB | 0' - 0" | 17.1 | 0' - 2 1/2" | 0' - 3" | 0' - 0 1/2" | 0' - 1" |
| 2L3X2-1/2X1/2X3/8LLBB | 5.01 in² | LLBB | 0' - 0 3/8" | 17.1 | 0' - 2 1/2" | 0' - 3" | 0' - 0 1/2" | 0' - 1" |
| 2L3X2-1/2X1/2X3/4LLBB | 5.01 in² | LLBB | 0' - 0 3/4" | 17.1 | 0' - 2 1/2" | 0' - 3" | 0' - 0 1/2" | 0' - 1" |
| 2L3X2-1/2X7/16LLBB | 4.44 in² | LLBB | 0' - 0" | 15.1 | 0' - 2 1/2" | 0' - 3" | 0' - 0 7/16" | 0' - 1" |
| 2L3X2-1/2X7/16X3/8LLBB | 4.44 in² | LLBB | 0' - 0 3/8" | 15.1 | 0' - 2 1/2" | 0' - 3" | 0' - 0 7/16" | 0' - 1" |
| 2L3X2-1/2X7/16X3/4LLBB | 4.44 in² | LLBB | 0' - 0 3/4" | 15.1 | 0' - 2 1/2" | 0' - 3" | 0' - 0 7/16" | 0' - 1" |
| 2L3X2-1/2X3/8LLBB | 3.86 in² | LLBB | 0' - 0" | 13.1 | 0' - 2 1/2" | 0' - 3" | 0' - 0 3/8" | 0' - 0 15/16" |
| 2L3X2-1/2X3/8X3/8LLBB | 3.86 in² | LLBB | 0' - 0 3/8" | 13.1 | 0' - 2 1/2" | 0' - 3" | 0' - 0 3/8" | 0' - 0 15/16" |
| 2L3X2-1/2X3/8X3/4LLBB | 3.86 in² | LLBB | 0' - 0 3/4" | 13.1 | 0' - 2 1/2" | 0' - 3" | 0' - 0 3/8" | 0' - 0 15/16" |
| 2L3X2-1/2X5/16LLBB | 3.25 in² | LLBB | 0' - 0" | 11.1 | 0' - 2 1/2" | 0' - 3" | 0' - 0 5/16" | 0' - 0 15/16" |
| 2L3X2-1/2X5/16X3/8LLBB | 3.25 in² | LLBB | 0' - 0 3/8" | 11.1 | 0' - 2 1/2" | 0' - 3" | 0' - 0 5/16" | 0' - 0 15/16" |
| 2L3X2-1/2X5/16X3/4LLBB | 3.25 in² | LLBB | 0' - 0 3/4" | 11.1 | 0' - 2 1/2" | 0' - 3" | 0' - 0 5/16" | 0' - 0 15/16" |
| 2L3X2-1/2X1/4LLBB | 2.64 in² | LLBB | 0' - 0" | 8.97 | 0' - 2 1/2" | 0' - 3" | 0' - 0 1/4" | 0' - 0 7/8" |
| 2L3X2-1/2X1/4X3/8LLBB | 2.64 in² | LLBB | 0' - 0 3/8" | 8.97 | 0' - 2 1/2" | 0' - 3" | 0' - 0 1/4" | 0' - 0 7/8" |
| 2L3X2-1/2X1/4X3/4LLBB | 2.64 in² | LLBB | 0' - 0 3/4" | 8.97 | 0' - 2 1/2" | 0' - 3" | 0' - 0 1/4" | 0' - 0 7/8" |
| 2L3X2-1/2X3/16LLBB | 2 in² | LLBB | 0' - 0" | 6.82 | 0' - 2 1/2" | 0' - 3" | 0' - 0 3/16" | 0' - 0 7/8" |
| 2L3X2-1/2X3/16X3/8LLBB | 2 in² | LLBB | 0' - 0 3/8" | 6.82 | 0' - 2 1/2" | 0' - 3" | 0' - 0 3/16" | 0' - 0 7/8" |
| 2L3X2-1/2X3/16X3/4LLBB | 2 in² | LLBB | 0' - 0 3/4" | 6.82 | 0' - 2 1/2" | 0' - 3" | 0' - 0 3/16" | 0' - 0 7/8" |
| 2L3X2X1/2LLBB | 4.53 in² | LLBB | 0' - 0" | 15.4 | 0' - 2" | 0' - 3" | 0' - 0 1/2" | 0' - 1 1/16" |
| 2L3X2X1/2X3/8LLBB | 4.53 in² | LLBB | 0' - 0 3/8" | 15.4 | 0' - 2" | 0' - 3" | 0' - 0 1/2" | 0' - 1 1/16" |
| 2L3X2X1/2X3/4LLBB | 4.53 in² | LLBB | 0' - 0 3/4" | 15.4 | 0' - 2" | 0' - 3" | 0' - 0 1/2" | 0' - 1 1/16" |
| 2L3X2X3/8LLBB | 3.5 in² | LLBB | 0' - 0" | 11.9 | 0' - 2" | 0' - 3" | 0' - 0 3/8" | 0' - 1" |
| 2L3X2X3/8X3/8LLBB | 3.5 in² | LLBB | 0' - 0 3/8" | 11.9 | 0' - 2" | 0' - 3" | 0' - 0 3/8" | 0' - 1" |
| 2L3X2X3/8X3/4LLBB | 3.5 in² | LLBB | 0' - 0 3/4" | 11.9 | 0' - 2" | 0' - 3" | 0' - 0 3/8" | 0' - 1" |
| 2L3X2X5/16LLBB | 2.96 in² | LLBB | 0' - 0" | 10.1 | 0' - 2" | 0' - 3" | 0' - 0 5/16" | 0' - 1" |
| 2L3X2X5/16X3/8LLBB | 2.96 in² | LLBB | 0' - 0 3/8" | 10.1 | 0' - 2" | 0' - 3" | 0' - 0 5/16" | 0' - 1" |
| 2L3X2X5/16X3/4LLBB | 2.96 in² | LLBB | 0' - 0 3/4" | 10.1 | 0' - 2" | 0' - 3" | 0' - 0 5/16" | 0' - 1" |
| 2L3X2X1/4LLBB | 2.4 in² | LLBB | 0' - 0" | 8.18 | 0' - 2" | 0' - 3" | 0' - 0 1/4" | 0' - 1" |
| 2L3X2X1/4X3/8LLBB | 2.4 in² | LLBB | 0' - 0 3/8" | 8.18 | 0' - 2" | 0' - 3" | 0' - 0 1/4" | 0' - 1" |
| 2L3X2X1/4X3/4LLBB | 2.4 in² | LLBB | 0' - 0 3/4" | 8.18 | 0' - 2" | 0' - 3" | 0' - 0 1/4" | 0' - 1" |
| 2L3X2X3/16LLBB | 1.83 in² | LLBB | 0' - 0" | 6.24 | 0' - 2" | 0' - 3" | 0' - 0 3/16" | 0' - 0 15/16" |
| 2L3X2X3/16X3/8LLBB | 1.83 in² | LLBB | 0' - 0 3/8" | 6.24 | 0' - 2" | 0' - 3" | 0' - 0 3/16" | 0' - 0 15/16" |
| 2L3X2X3/16X3/4LLBB | 1.83 in² | LLBB | 0' - 0 3/4" | 6.24 | 0' - 2" | 0' - 3" | 0' - 0 3/16" | 0' - 0 15/16" |
| 2L2-1/2X2X3/8LLBB | 3.11 in² | LLBB | 0' - 0" | 10.6 | 0' - 2" | 0' - 2 1/2" | 0' - 0 3/8" | 0' - 0 13/16" |
| 2L2-1/2X2X3/8X3/8LLBB | 3.11 in² | LLBB | 0' - 0 3/8" | 10.6 | 0' - 2" | 0' - 2 1/2" | 0' - 0 3/8" | 0' - 0 13/16" |
| 2L2-1/2X2X3/8X3/4LLBB | 3.11 in² | LLBB | 0' - 0 3/4" | 10.6 | 0' - 2" | 0' - 2 1/2" | 0' - 0 3/8" | 0' - 0 13/16" |
| 2L2-1/2X2X5/16LLBB | 2.64 in² | LLBB | 0' - 0" | 8.97 | 0' - 2" | 0' - 2 1/2" | 0' - 0 5/16" | 0' - 0 13/16" |
| 2L2-1/2X2X5/16X3/8LLBB | 2.64 in² | LLBB | 0' - 0 3/8" | 8.97 | 0' - 2" | 0' - 2 1/2" | 0' - 0 5/16" | 0' - 0 13/16" |
| 2L2-1/2X2X5/16X3/4LLBB | 2.64 in² | LLBB | 0' - 0 3/4" | 8.97 | 0' - 2" | 0' - 2 1/2" | 0' - 0 5/16" | 0' - 0 13/16" |
| 2L2-1/2X2X1/4LLBB | 2.14 in² | LLBB | 0' - 0" | 7.3 | 0' - 2" | 0' - 2 1/2" | 0' - 0 1/4" | 0' - 0 3/4" |
| 2L2-1/2X2X1/4X3/8LLBB | 2.14 in² | LLBB | 0' - 0 3/8" | 7.3 | 0' - 2" | 0' - 2 1/2" | 0' - 0 1/4" | 0' - 0 3/4" |
| 2L2-1/2X2X1/4X3/4LLBB | 2.14 in² | LLBB | 0' - 0 3/4" | 7.3 | 0' - 2" | 0' - 2 1/2" | 0' - 0 1/4" | 0' - 0 3/4" |
| 2L2-1/2X2X3/16LLBB | 1.64 in² | LLBB | 0' - 0" | 5.57 | 0' - 2" | 0' - 2 1/2" | 0' - 0 3/16" | 0' - 0 3/4" |
| 2L2-1/2X2X3/16X3/8LLBB | 1.64 in² | LLBB | 0' - 0 3/8" | 5.57 | 0' - 2" | 0' - 2 1/2" | 0' - 0 3/16" | 0' - 0 3/4" |
| 2L2-1/2X2X3/16X3/4LLBB | 1.64 in² | LLBB | 0' - 0 3/4" | 5.57 | 0' - 2" | 0' - 2 1/2" | 0' - 0 3/16" | 0' - 0 3/4" |
| 2L8X6X1SLBB | 26.1 in² | SLBB | 0' - 0" | 88.8 | 0' - 8" | 0' - 6" | 0' - 1" | 0' - 1 5/8" |
| 2L8X6X1X3/8SLBB | 26.1 in² | SLBB | 0' - 0 3/8" | 88.8 | 0' - 8" | 0' - 6" | 0' - 1" | 0' - 1 5/8" |
| 2L8X6X1X3/4SLBB | 26.1 in² | SLBB | 0' - 0 3/4" | 88.8 | 0' - 8" | 0' - 6" | 0' - 1" | 0' - 1 5/8" |
| 2L8X6X7/8SLBB | 23.1 in² | SLBB | 0' - 0" | 78.5 | 0' - 8" | 0' - 6" | 0' - 0 7/8" | 0' - 1 5/8" |
| 2L8X6X7/8X3/8SLBB | 23.1 in² | SLBB | 0' - 0 3/8" | 78.5 | 0' - 8" | 0' - 6" | 0' - 0 7/8" | 0' - 1 5/8" |
| 2L8X6X7/8X3/4SLBB | 23.1 in² | SLBB | 0' - 0 3/4" | 78.5 | 0' - 8" | 0' - 6" | 0' - 0 7/8" | 0' - 1 5/8" |
| 2L8X6X3/4SLBB | 20 in² | SLBB | 0' - 0" | 68 | 0' - 8" | 0' - 6" | 0' - 0 3/4" | 0' - 1 9/16" |
| 2L8X6X3/4X3/8SLBB | 20 in² | SLBB | 0' - 0 3/8" | 68 | 0' - 8" | 0' - 6" | 0' - 0 3/4" | 0' - 1 9/16" |
| 2L8X6X3/4X3/4SLBB | 20 in² | SLBB | 0' - 0 3/4" | 68 | 0' - 8" | 0' - 6" | 0' - 0 3/4" | 0' - 1 9/16" |
| 2L8X6X5/8SLBB | 16.8 in² | SLBB | 0' - 0" | 57.3 | 0' - 8" | 0' - 6" | 0' - 0 5/8" | 0' - 1 1/2" |
| 2L8X6X5/8X3/8SLBB | 16.8 in² | SLBB | 0' - 0 3/8" | 57.3 | 0' - 8" | 0' - 6" | 0' - 0 5/8" | 0' - 1 1/2" |
| 2L8X6X5/8X3/4SLBB | 16.8 in² | SLBB | 0' - 0 3/4" | 57.3 | 0' - 8" | 0' - 6" | 0' - 0 5/8" | 0' - 1 1/2" |
| 2L8X6X9/16SLBB | 15.2 in² | SLBB | 0' - 0" | 51.8 | 0' - 8" | 0' - 6" | 0' - 0 9/16" | 0' - 1 1/2" |
| 2L8X6X9/16X3/8SLBB | 15.2 in² | SLBB | 0' - 0 3/8" | 51.8 | 0' - 8" | 0' - 6" | 0' - 0 9/16" | 0' - 1 1/2" |
| 2L8X6X9/16X3/4SLBB | 15.2 in² | SLBB | 0' - 0 3/4" | 51.8 | 0' - 8" | 0' - 6" | 0' - 0 9/16" | 0' - 1 1/2" |
| 2L8X6X1/2SLBB | 13.6 in² | SLBB | 0' - 0" | 46.3 | 0' - 8" | 0' - 6" | 0' - 0 1/2" | 0' - 1 7/16" |
| 2L8X6X1/2X3/8SLBB | 13.6 in² | SLBB | 0' - 0 3/8" | 46.3 | 0' - 8" | 0' - 6" | 0' - 0 1/2" | 0' - 1 7/16" |
| 2L8X6X1/2X3/4SLBB | 13.6 in² | SLBB | 0' - 0 3/4" | 46.3 | 0' - 8" | 0' - 6" | 0' - 0 1/2" | 0' - 1 7/16" |
| 2L8X6X7/16SLBB | 12 in² | SLBB | 0' - 0" | 40.7 | 0' - 8" | 0' - 6" | 0' - 0 7/16" | 0' - 1 7/16" |
| 2L8X6X7/16X3/8SLBB | 12 in² | SLBB | 0' - 0 3/8" | 40.7 | 0' - 8" | 0' - 6" | 0' - 0 7/16" | 0' - 1 7/16" |
| 2L8X6X7/16X3/4SLBB | 12 in² | SLBB | 0' - 0 3/4" | 40.7 | 0' - 8" | 0' - 6" | 0' - 0 7/16" | 0' - 1 7/16" |
| 2L8X4X1SLBB | 22.1 in² | SLBB | 0' - 0" | 75.2 | 0' - 8" | 0' - 4" | 0' - 1" | 0' - 1 1/16" |
| 2L8X4X1X3/8SLBB | 22.1 in² | SLBB | 0' - 0 3/8" | 75.2 | 0' - 8" | 0' - 4" | 0' - 1" | 0' - 1 1/16" |
| 2L8X4X1X3/4SLBB | 22.1 in² | SLBB | 0' - 0 3/4" | 75.2 | 0' - 8" | 0' - 4" | 0' - 1" | 0' - 1 1/16" |
| 2L8X4X7/8SLBB | 19.6 in² | SLBB | 0' - 0" | 66.6 | 0' - 8" | 0' - 4" | 0' - 0 7/8" | 0' - 1" |
| 2L8X4X7/8X3/8SLBB | 19.6 in² | SLBB | 0' - 0 3/8" | 66.6 | 0' - 8" | 0' - 4" | 0' - 0 7/8" | 0' - 1" |
| 2L8X4X7/8X3/4SLBB | 19.6 in² | SLBB | 0' - 0 3/4" | 66.6 | 0' - 8" | 0' - 4" | 0' - 0 7/8" | 0' - 1" |
| 2L8X4X3/4SLBB | 17 in² | SLBB | 0' - 0" | 57.8 | 0' - 8" | 0' - 4" | 0' - 0 3/4" | 0' - 0 15/16" |
| 2L8X4X3/4X3/8SLBB | 17 in² | SLBB | 0' - 0 3/8" | 57.8 | 0' - 8" | 0' - 4" | 0' - 0 3/4" | 0' - 0 15/16" |
| 2L8X4X3/4X3/4SLBB | 17 in² | SLBB | 0' - 0 3/4" | 57.8 | 0' - 8" | 0' - 4" | 0' - 0 3/4" | 0' - 0 15/16" |
| 2L8X4X5/8SLBB | 14.3 in² | SLBB | 0' - 0" | 48.7 | 0' - 8" | 0' - 4" | 0' - 0 5/8" | 0' - 0 7/8" |
| 2L8X4X5/8X3/8SLBB | 14.3 in² | SLBB | 0' - 0 3/8" | 48.7 | 0' - 8" | 0' - 4" | 0' - 0 5/8" | 0' - 0 7/8" |
| 2L8X4X5/8X3/4SLBB | 14.3 in² | SLBB | 0' - 0 3/4" | 48.7 | 0' - 8" | 0' - 4" | 0' - 0 5/8" | 0' - 0 7/8" |
| 2L8X4X9/16SLBB | 13 in² | SLBB | 0' - 0" | 44.1 | 0' - 8" | 0' - 4" | 0' - 0 9/16" | 0' - 0 7/8" |
| 2L8X4X9/16X3/8SLBB | 13 in² | SLBB | 0' - 0 3/8" | 44.1 | 0' - 8" | 0' - 4" | 0' - 0 9/16" | 0' - 0 7/8" |
| 2L8X4X9/16X3/4SLBB | 13 in² | SLBB | 0' - 0 3/4" | 44.1 | 0' - 8" | 0' - 4" | 0' - 0 9/16" | 0' - 0 7/8" |
| 2L8X4X1/2SLBB | 11.6 in² | SLBB | 0' - 0" | 39.5 | 0' - 8" | 0' - 4" | 0' - 0 1/2" | 0' - 0 7/8" |
| 2L8X4X1/2X3/8SLBB | 11.6 in² | SLBB | 0' - 0 3/8" | 39.5 | 0' - 8" | 0' - 4" | 0' - 0 1/2" | 0' - 0 7/8" |
| 2L8X4X1/2X3/4SLBB | 11.6 in² | SLBB | 0' - 0 3/4" | 39.5 | 0' - 8" | 0' - 4" | 0' - 0 1/2" | 0' - 0 7/8" |
| 2L8X4X7/16SLBB | 10.2 in² | SLBB | 0' - 0" | 34.8 | 0' - 8" | 0' - 4" | 0' - 0 7/16" | 0' - 0 13/16" |
| 2L8X4X7/16X3/8SLBB | 10.2 in² | SLBB | 0' - 0 3/8" | 34.8 | 0' - 8" | 0' - 4" | 0' - 0 7/16" | 0' - 0 13/16" |
| 2L8X4X7/16X3/4SLBB | 10.2 in² | SLBB | 0' - 0 3/4" | 34.8 | 0' - 8" | 0' - 4" | 0' - 0 7/16" | 0' - 0 13/16" |
| 2L7X4X3/4SLBB | 15.4 in² | SLBB | 0' - 0" | 52.4 | 0' - 7" | 0' - 4" | 0' - 0 3/4" | 0' - 1" |
| 2L7X4X3/4X3/8SLBB | 15.4 in² | SLBB | 0' - 0 3/8" | 52.4 | 0' - 7" | 0' - 4" | 0' - 0 3/4" | 0' - 1" |
| 2L7X4X3/4X3/4SLBB | 15.4 in² | SLBB | 0' - 0 3/4" | 52.4 | 0' - 7" | 0' - 4" | 0' - 0 3/4" | 0' - 1" |
| 2L7X4X5/8SLBB | 13 in² | SLBB | 0' - 0" | 44.2 | 0' - 7" | 0' - 4" | 0' - 0 5/8" | 0' - 0 15/16" |
| 2L7X4X5/8X3/8SLBB | 13 in² | SLBB | 0' - 0 3/8" | 44.2 | 0' - 7" | 0' - 4" | 0' - 0 5/8" | 0' - 0 15/16" |
| 2L7X4X5/8X3/4SLBB | 13 in² | SLBB | 0' - 0 3/4" | 44.2 | 0' - 7" | 0' - 4" | 0' - 0 5/8" | 0' - 0 15/16" |
| 2L7X4X1/2SLBB | 10.5 in² | SLBB | 0' - 0" | 35.8 | 0' - 7" | 0' - 4" | 0' - 0 1/2" | 0' - 0 15/16" |
| 2L7X4X1/2X3/8SLBB | 10.5 in² | SLBB | 0' - 0 3/8" | 35.8 | 0' - 7" | 0' - 4" | 0' - 0 1/2" | 0' - 0 15/16" |
| 2L7X4X1/2X3/4SLBB | 10.5 in² | SLBB | 0' - 0 3/4" | 35.8 | 0' - 7" | 0' - 4" | 0' - 0 1/2" | 0' - 0 15/16" |
| 2L7X4X7/16SLBB | 9.27 in² | SLBB | 0' - 0" | 31.5 | 0' - 7" | 0' - 4" | 0' - 0 7/16" | 0' - 0 7/8" |
| 2L7X4X7/16X3/8SLBB | 9.27 in² | SLBB | 0' - 0 3/8" | 31.5 | 0' - 7" | 0' - 4" | 0' - 0 7/16" | 0' - 0 7/8" |
| 2L7X4X7/16X3/4SLBB | 9.27 in² | SLBB | 0' - 0 3/4" | 31.5 | 0' - 7" | 0' - 4" | 0' - 0 7/16" | 0' - 0 7/8" |
| 2L7X4X3/8SLBB | 8 in² | SLBB | 0' - 0" | 27.2 | 0' - 7" | 0' - 4" | 0' - 0 3/8" | 0' - 0 7/8" |
| 2L7X4X3/8X3/8SLBB | 8 in² | SLBB | 0' - 0 3/8" | 27.2 | 0' - 7" | 0' - 4" | 0' - 0 3/8" | 0' - 0 7/8" |
| 2L7X4X3/8X3/4SLBB | 8 in² | SLBB | 0' - 0 3/4" | 27.2 | 0' - 7" | 0' - 4" | 0' - 0 3/8" | 0' - 0 7/8" |
| 2L6X4X7/8SLBB | 16 in² | SLBB | 0' - 0" | 54.3 | 0' - 6" | 0' - 4" | 0' - 0 7/8" | 0' - 1 1/8" |
| 2L6X4X7/8X3/8SLBB | 16 in² | SLBB | 0' - 0 3/8" | 54.3 | 0' - 6" | 0' - 4" | 0' - 0 7/8" | 0' - 1 1/8" |
| 2L6X4X7/8X3/4SLBB | 16 in² | SLBB | 0' - 0 3/4" | 54.3 | 0' - 6" | 0' - 4" | 0' - 0 7/8" | 0' - 1 1/8" |
| 2L6X4X3/4SLBB | 13.9 in² | SLBB | 0' - 0" | 47.2 | 0' - 6" | 0' - 4" | 0' - 0 3/4" | 0' - 1 1/16" |
| 2L6X4X3/4X3/8SLBB | 13.9 in² | SLBB | 0' - 0 3/8" | 47.2 | 0' - 6" | 0' - 4" | 0' - 0 3/4" | 0' - 1 1/16" |
| 2L6X4X3/4X3/4SLBB | 13.9 in² | SLBB | 0' - 0 3/4" | 47.2 | 0' - 6" | 0' - 4" | 0' - 0 3/4" | 0' - 1 1/16" |
| 2L6X4X5/8SLBB | 11.7 in² | SLBB | 0' - 0" | 39.9 | 0' - 6" | 0' - 4" | 0' - 0 5/8" | 0' - 1" |
| 2L6X4X5/8X3/8SLBB | 11.7 in² | SLBB | 0' - 0 3/8" | 39.9 | 0' - 6" | 0' - 4" | 0' - 0 5/8" | 0' - 1" |
| 2L6X4X5/8X3/4SLBB | 11.7 in² | SLBB | 0' - 0 3/4" | 39.9 | 0' - 6" | 0' - 4" | 0' - 0 5/8" | 0' - 1" |
| 2L6X4X9/16SLBB | 10.6 in² | SLBB | 0' - 0" | 36.1 | 0' - 6" | 0' - 4" | 0' - 0 9/16" | 0' - 1" |
| 2L6X4X9/16X3/8SLBB | 10.6 in² | SLBB | 0' - 0 3/8" | 36.1 | 0' - 6" | 0' - 4" | 0' - 0 9/16" | 0' - 1" |
| 2L6X4X9/16X3/4SLBB | 10.6 in² | SLBB | 0' - 0 3/4" | 36.1 | 0' - 6" | 0' - 4" | 0' - 0 9/16" | 0' - 1" |
| 2L6X4X1/2SLBB | 9.5 in² | SLBB | 0' - 0" | 32.3 | 0' - 6" | 0' - 4" | 0' - 0 1/2" | 0' - 1" |
| 2L6X4X1/2X3/8SLBB | 9.5 in² | SLBB | 0' - 0 3/8" | 32.3 | 0' - 6" | 0' - 4" | 0' - 0 1/2" | 0' - 1" |
| 2L6X4X1/2X3/4SLBB | 9.5 in² | SLBB | 0' - 0 3/4" | 32.3 | 0' - 6" | 0' - 4" | 0' - 0 1/2" | 0' - 1" |
| 2L6X4X7/16SLBB | 8.36 in² | SLBB | 0' - 0" | 28.5 | 0' - 6" | 0' - 4" | 0' - 0 7/16" | 0' - 0 15/16" |
| 2L6X4X7/16X3/8SLBB | 8.36 in² | SLBB | 0' - 0 3/8" | 28.5 | 0' - 6" | 0' - 4" | 0' - 0 7/16" | 0' - 0 15/16" |
| 2L6X4X7/16X3/4SLBB | 8.36 in² | SLBB | 0' - 0 3/4" | 28.5 | 0' - 6" | 0' - 4" | 0' - 0 7/16" | 0' - 0 15/16" |
| 2L6X4X3/8SLBB | 7.22 in² | SLBB | 0' - 0" | 24.6 | 0' - 6" | 0' - 4" | 0' - 0 3/8" | 0' - 0 15/16" |
| 2L6X4X3/8X3/8SLBB | 7.22 in² | SLBB | 0' - 0 3/8" | 24.6 | 0' - 6" | 0' - 4" | 0' - 0 3/8" | 0' - 0 15/16" |
| 2L6X4X3/8X3/4SLBB | 7.22 in² | SLBB | 0' - 0 3/4" | 24.6 | 0' - 6" | 0' - 4" | 0' - 0 3/8" | 0' - 0 15/16" |
| 2L6X4X5/16SLBB | 6.05 in² | SLBB | 0' - 0" | 20.6 | 0' - 6" | 0' - 4" | 0' - 0 5/16" | 0' - 0 15/16" |
| 2L6X4X5/16X3/8SLBB | 6.05 in² | SLBB | 0' - 0 3/8" | 20.6 | 0' - 6" | 0' - 4" | 0' - 0 5/16" | 0' - 0 15/16" |
| 2L6X4X5/16X3/4SLBB | 6.05 in² | SLBB | 0' - 0 3/4" | 20.6 | 0' - 6" | 0' - 4" | 0' - 0 5/16" | 0' - 0 15/16" |
| 2L6X3-1/2X1/2SLBB | 9.04 in² | SLBB | 0' - 0" | 30.7 | 0' - 6" | 0' - 3 1/2" | 0' - 0 1/2" | 0' - 0 13/16" |
| 2L6X3-1/2X1/2X3/8SLBB | 9.04 in² | SLBB | 0' - 0 3/8" | 30.7 | 0' - 6" | 0' - 3 1/2" | 0' - 0 1/2" | 0' - 0 13/16" |
| 2L6X3-1/2X1/2X3/4SLBB | 9.04 in² | SLBB | 0' - 0 3/4" | 30.7 | 0' - 6" | 0' - 3 1/2" | 0' - 0 1/2" | 0' - 0 13/16" |
| 2L6X3-1/2X3/8SLBB | 6.88 in² | SLBB | 0' - 0" | 23.4 | 0' - 6" | 0' - 3 1/2" | 0' - 0 3/8" | 0' - 0 3/4" |
| 2L6X3-1/2X3/8X3/8SLBB | 6.88 in² | SLBB | 0' - 0 3/8" | 23.4 | 0' - 6" | 0' - 3 1/2" | 0' - 0 3/8" | 0' - 0 3/4" |
| 2L6X3-1/2X3/8X3/4SLBB | 6.88 in² | SLBB | 0' - 0 3/4" | 23.4 | 0' - 6" | 0' - 3 1/2" | 0' - 0 3/8" | 0' - 0 3/4" |
| 2L6X3-1/2X5/16SLBB | 5.78 in² | SLBB | 0' - 0" | 19.7 | 0' - 6" | 0' - 3 1/2" | 0' - 0 5/16" | 0' - 0 3/4" |
| 2L6X3-1/2X5/16X3/8SLBB | 5.78 in² | SLBB | 0' - 0 3/8" | 19.7 | 0' - 6" | 0' - 3 1/2" | 0' - 0 5/16" | 0' - 0 3/4" |
| 2L6X3-1/2X5/16X3/4SLBB | 5.78 in² | SLBB | 0' - 0 3/4" | 19.7 | 0' - 6" | 0' - 3 1/2" | 0' - 0 5/16" | 0' - 0 3/4" |
| 2L5X3-1/2X3/4SLBB | 11.6 in² | SLBB | 0' - 0" | 39.6 | 0' - 5" | 0' - 3 1/2" | 0' - 0 3/4" | 0' - 1" |
| 2L5X3-1/2X3/4X3/8SLBB | 11.6 in² | SLBB | 0' - 0 3/8" | 39.6 | 0' - 5" | 0' - 3 1/2" | 0' - 0 3/4" | 0' - 1" |
| 2L5X3-1/2X3/4X3/4SLBB | 11.6 in² | SLBB | 0' - 0 3/4" | 39.6 | 0' - 5" | 0' - 3 1/2" | 0' - 0 3/4" | 0' - 1" |
| 2L5X3-1/2X5/8SLBB | 9.85 in² | SLBB | 0' - 0" | 33.5 | 0' - 5" | 0' - 3 1/2" | 0' - 0 5/8" | 0' - 0 15/16" |
| 2L5X3-1/2X5/8X3/8SLBB | 9.85 in² | SLBB | 0' - 0 3/8" | 33.5 | 0' - 5" | 0' - 3 1/2" | 0' - 0 5/8" | 0' - 0 15/16" |
| 2L5X3-1/2X5/8X3/4SLBB | 9.85 in² | SLBB | 0' - 0 3/4" | 33.5 | 0' - 5" | 0' - 3 1/2" | 0' - 0 5/8" | 0' - 0 15/16" |
| 2L5X3-1/2X1/2SLBB | 8.01 in² | SLBB | 0' - 0" | 27.2 | 0' - 5" | 0' - 3 1/2" | 0' - 0 1/2" | 0' - 0 7/8" |
| 2L5X3-1/2X1/2X3/8SLBB | 8.01 in² | SLBB | 0' - 0 3/8" | 27.2 | 0' - 5" | 0' - 3 1/2" | 0' - 0 1/2" | 0' - 0 7/8" |
| 2L5X3-1/2X1/2X3/4SLBB | 8.01 in² | SLBB | 0' - 0 3/4" | 27.2 | 0' - 5" | 0' - 3 1/2" | 0' - 0 1/2" | 0' - 0 7/8" |
| 2L5X3-1/2X3/8SLBB | 6.1 in² | SLBB | 0' - 0" | 20.8 | 0' - 5" | 0' - 3 1/2" | 0' - 0 3/8" | 0' - 0 7/8" |
| 2L5X3-1/2X3/8X3/8SLBB | 6.1 in² | SLBB | 0' - 0 3/8" | 20.8 | 0' - 5" | 0' - 3 1/2" | 0' - 0 3/8" | 0' - 0 7/8" |
| 2L5X3-1/2X3/8X3/4SLBB | 6.1 in² | SLBB | 0' - 0 3/4" | 20.8 | 0' - 5" | 0' - 3 1/2" | 0' - 0 3/8" | 0' - 0 7/8" |
| 2L5X3-1/2X5/16SLBB | 5.12 in² | SLBB | 0' - 0" | 17.4 | 0' - 5" | 0' - 3 1/2" | 0' - 0 5/16" | 0' - 0 13/16" |
| 2L5X3-1/2X5/16X3/8SLBB | 5.12 in² | SLBB | 0' - 0 3/8" | 17.4 | 0' - 5" | 0' - 3 1/2" | 0' - 0 5/16" | 0' - 0 13/16" |
| 2L5X3-1/2X5/16X3/4SLBB | 5.12 in² | SLBB | 0' - 0 3/4" | 17.4 | 0' - 5" | 0' - 3 1/2" | 0' - 0 5/16" | 0' - 0 13/16" |
| 2L5X3-1/2X1/4SLBB | 4.13 in² | SLBB | 0' - 0" | 14.1 | 0' - 5" | 0' - 3 1/2" | 0' - 0 1/4" | 0' - 0 13/16" |
| 2L5X3-1/2X1/4X3/8SLBB | 4.13 in² | SLBB | 0' - 0 3/8" | 14.1 | 0' - 5" | 0' - 3 1/2" | 0' - 0 1/4" | 0' - 0 13/16" |
| 2L5X3-1/2X1/4X3/4SLBB | 4.13 in² | SLBB | 0' - 0 3/4" | 14.1 | 0' - 5" | 0' - 3 1/2" | 0' - 0 1/4" | 0' - 0 13/16" |
| 2L5X3X1/2SLBB | 7.51 in² | SLBB | 0' - 0" | 25.5 | 0' - 5" | 0' - 3" | 0' - 0 1/2" | 0' - 0 3/4" |
| 2L5X3X1/2X3/8SLBB | 7.51 in² | SLBB | 0' - 0 3/8" | 25.5 | 0' - 5" | 0' - 3" | 0' - 0 1/2" | 0' - 0 3/4" |
| 2L5X3X1/2X3/4SLBB | 7.51 in² | SLBB | 0' - 0 3/4" | 25.5 | 0' - 5" | 0' - 3" | 0' - 0 1/2" | 0' - 0 3/4" |
| 2L5X3X7/16SLBB | 6.62 in² | SLBB | 0' - 0" | 22.5 | 0' - 5" | 0' - 3" | 0' - 0 7/16" | 0' - 0 3/4" |
| 2L5X3X7/16X3/8SLBB | 6.62 in² | SLBB | 0' - 0 3/8" | 22.5 | 0' - 5" | 0' - 3" | 0' - 0 7/16" | 0' - 0 3/4" |
| 2L5X3X7/16X3/4SLBB | 6.62 in² | SLBB | 0' - 0 3/4" | 22.5 | 0' - 5" | 0' - 3" | 0' - 0 7/16" | 0' - 0 3/4" |
| 2L5X3X3/8SLBB | 5.73 in² | SLBB | 0' - 0" | 19.5 | 0' - 5" | 0' - 3" | 0' - 0 3/8" | 0' - 0 11/16" |
| 2L5X3X3/8X3/8SLBB | 5.73 in² | SLBB | 0' - 0 3/8" | 19.5 | 0' - 5" | 0' - 3" | 0' - 0 3/8" | 0' - 0 11/16" |
| 2L5X3X3/8X3/4SLBB | 5.73 in² | SLBB | 0' - 0 3/4" | 19.5 | 0' - 5" | 0' - 3" | 0' - 0 3/8" | 0' - 0 11/16" |
| 2L5X3X5/16SLBB | 4.81 in² | SLBB | 0' - 0" | 16.4 | 0' - 5" | 0' - 3" | 0' - 0 5/16" | 0' - 0 11/16" |
| 2L5X3X5/16X3/8SLBB | 4.81 in² | SLBB | 0' - 0 3/8" | 16.4 | 0' - 5" | 0' - 3" | 0' - 0 5/16" | 0' - 0 11/16" |
| 2L5X3X5/16X3/4SLBB | 4.81 in² | SLBB | 0' - 0 3/4" | 16.4 | 0' - 5" | 0' - 3" | 0' - 0 5/16" | 0' - 0 11/16" |
| 2L5X3X1/4SLBB | 3.88 in² | SLBB | 0' - 0" | 13.2 | 0' - 5" | 0' - 3" | 0' - 0 1/4" | 0' - 0 5/8" |
| 2L5X3X1/4X3/8SLBB | 3.88 in² | SLBB | 0' - 0 3/8" | 13.2 | 0' - 5" | 0' - 3" | 0' - 0 1/4" | 0' - 0 5/8" |
| 2L5X3X1/4X3/4SLBB | 3.88 in² | SLBB | 0' - 0 3/4" | 13.2 | 0' - 5" | 0' - 3" | 0' - 0 1/4" | 0' - 0 5/8" |
| 2L4X3-1/2X1/2SLBB | 7.01 in² | SLBB | 0' - 0" | 23.8 | 0' - 4" | 0' - 3 1/2" | 0' - 0 1/2" | 0' - 1" |
| 2L4X3-1/2X1/2X3/8SLBB | 7.01 in² | SLBB | 0' - 0 3/8" | 23.8 | 0' - 4" | 0' - 3 1/2" | 0' - 0 1/2" | 0' - 1" |
| 2L4X3-1/2X1/2X3/4SLBB | 7.01 in² | SLBB | 0' - 0 3/4" | 23.8 | 0' - 4" | 0' - 3 1/2" | 0' - 0 1/2" | 0' - 1" |
| 2L4X3-1/2X3/8SLBB | 5.35 in² | SLBB | 0' - 0" | 18.2 | 0' - 4" | 0' - 3 1/2" | 0' - 0 3/8" | 0' - 0 15/16" |
| 2L4X3-1/2X3/8X3/8SLBB | 5.35 in² | SLBB | 0' - 0 3/8" | 18.2 | 0' - 4" | 0' - 3 1/2" | 0' - 0 3/8" | 0' - 0 15/16" |
| 2L4X3-1/2X3/8X3/4SLBB | 5.35 in² | SLBB | 0' - 0 3/4" | 18.2 | 0' - 4" | 0' - 3 1/2" | 0' - 0 3/8" | 0' - 0 15/16" |
| 2L4X3-1/2X5/16SLBB | 4.5 in² | SLBB | 0' - 0" | 15.3 | 0' - 4" | 0' - 3 1/2" | 0' - 0 5/16" | 0' - 0 15/16" |
| 2L4X3-1/2X5/16X3/8SLBB | 4.5 in² | SLBB | 0' - 0 3/8" | 15.3 | 0' - 4" | 0' - 3 1/2" | 0' - 0 5/16" | 0' - 0 15/16" |
| 2L4X3-1/2X5/16X3/4SLBB | 4.5 in² | SLBB | 0' - 0 3/4" | 15.3 | 0' - 4" | 0' - 3 1/2" | 0' - 0 5/16" | 0' - 0 15/16" |
| 2L4X3-1/2X1/4SLBB | 3.63 in² | SLBB | 0' - 0" | 12.4 | 0' - 4" | 0' - 3 1/2" | 0' - 0 1/4" | 0' - 0 7/8" |
| 2L4X3-1/2X1/4X3/8SLBB | 3.63 in² | SLBB | 0' - 0 3/8" | 12.4 | 0' - 4" | 0' - 3 1/2" | 0' - 0 1/4" | 0' - 0 7/8" |
| 2L4X3-1/2X1/4X3/4SLBB | 3.63 in² | SLBB | 0' - 0 3/4" | 12.4 | 0' - 4" | 0' - 3 1/2" | 0' - 0 1/4" | 0' - 0 7/8" |
| 2L4X3X5/8SLBB | 7.98 in² | SLBB | 0' - 0" | 27.1 | 0' - 4" | 0' - 3" | 0' - 0 5/8" | 0' - 0 7/8" |
| 2L4X3X5/8X3/8SLBB | 7.98 in² | SLBB | 0' - 0 3/8" | 27.1 | 0' - 4" | 0' - 3" | 0' - 0 5/8" | 0' - 0 7/8" |
| 2L4X3X5/8X3/4SLBB | 7.98 in² | SLBB | 0' - 0 3/4" | 27.1 | 0' - 4" | 0' - 3" | 0' - 0 5/8" | 0' - 0 7/8" |
| 2L4X3X1/2SLBB | 6.51 in² | SLBB | 0' - 0" | 22.1 | 0' - 4" | 0' - 3" | 0' - 0 1/2" | 0' - 0 13/16" |
| 2L4X3X1/2X3/8SLBB | 6.51 in² | SLBB | 0' - 0 3/8" | 22.1 | 0' - 4" | 0' - 3" | 0' - 0 1/2" | 0' - 0 13/16" |
| 2L4X3X1/2X3/4SLBB | 6.51 in² | SLBB | 0' - 0 3/4" | 22.1 | 0' - 4" | 0' - 3" | 0' - 0 1/2" | 0' - 0 13/16" |
| 2L4X3X3/8SLBB | 4.98 in² | SLBB | 0' - 0" | 16.9 | 0' - 4" | 0' - 3" | 0' - 0 3/8" | 0' - 0 3/4" |
| 2L4X3X3/8X3/8SLBB | 4.98 in² | SLBB | 0' - 0 3/8" | 16.9 | 0' - 4" | 0' - 3" | 0' - 0 3/8" | 0' - 0 3/4" |
| 2L4X3X3/8X3/4SLBB | 4.98 in² | SLBB | 0' - 0 3/4" | 16.9 | 0' - 4" | 0' - 3" | 0' - 0 3/8" | 0' - 0 3/4" |
| 2L4X3X5/16SLBB | 4.19 in² | SLBB | 0' - 0" | 14.2 | 0' - 4" | 0' - 3" | 0' - 0 5/16" | 0' - 0 3/4" |
| 2L4X3X5/16X3/8SLBB | 4.19 in² | SLBB | 0' - 0 3/8" | 14.2 | 0' - 4" | 0' - 3" | 0' - 0 5/16" | 0' - 0 3/4" |
| 2L4X3X5/16X3/4SLBB | 4.19 in² | SLBB | 0' - 0 3/4" | 14.2 | 0' - 4" | 0' - 3" | 0' - 0 5/16" | 0' - 0 3/4" |
| 2L4X3X1/4SLBB | 3.38 in² | SLBB | 0' - 0" | 11.5 | 0' - 4" | 0' - 3" | 0' - 0 1/4" | 0' - 0 3/4" |
| 2L4X3X1/4X3/8SLBB | 3.38 in² | SLBB | 0' - 0 3/8" | 11.5 | 0' - 4" | 0' - 3" | 0' - 0 1/4" | 0' - 0 3/4" |
| 2L4X3X1/4X3/4SLBB | 3.38 in² | SLBB | 0' - 0 3/4" | 11.5 | 0' - 4" | 0' - 3" | 0' - 0 1/4" | 0' - 0 3/4" |
| 2L3-1/2X3X1/2SLBB | 6.04 in² | SLBB | 0' - 0" | 20.6 | 0' - 3 1/2" | 0' - 3" | 0' - 0 1/2" | 0' - 0 7/8" |
| 2L3-1/2X3X1/2X3/8SLBB | 6.04 in² | SLBB | 0' - 0 3/8" | 20.6 | 0' - 3 1/2" | 0' - 3" | 0' - 0 1/2" | 0' - 0 7/8" |
| 2L3-1/2X3X1/2X3/4SLBB | 6.04 in² | SLBB | 0' - 0 3/4" | 20.6 | 0' - 3 1/2" | 0' - 3" | 0' - 0 1/2" | 0' - 0 7/8" |
| 2L3-1/2X3X7/16SLBB | 5.34 in² | SLBB | 0' - 0" | 18.2 | 0' - 3 1/2" | 0' - 3" | 0' - 0 7/16" | 0' - 0 7/8" |
| 2L3-1/2X3X7/16X3/8SLBB | 5.34 in² | SLBB | 0' - 0 3/8" | 18.2 | 0' - 3 1/2" | 0' - 3" | 0' - 0 7/16" | 0' - 0 7/8" |
| 2L3-1/2X3X7/16X3/4SLBB | 5.34 in² | SLBB | 0' - 0 3/4" | 18.2 | 0' - 3 1/2" | 0' - 3" | 0' - 0 7/16" | 0' - 0 7/8" |
| 2L3-1/2X3X3/8SLBB | 4.63 in² | SLBB | 0' - 0" | 15.8 | 0' - 3 1/2" | 0' - 3" | 0' - 0 3/8" | 0' - 0 13/16" |
| 2L3-1/2X3X3/8X3/8SLBB | 4.63 in² | SLBB | 0' - 0 3/8" | 15.8 | 0' - 3 1/2" | 0' - 3" | 0' - 0 3/8" | 0' - 0 13/16" |
| 2L3-1/2X3X3/8X3/4SLBB | 4.63 in² | SLBB | 0' - 0 3/4" | 15.8 | 0' - 3 1/2" | 0' - 3" | 0' - 0 3/8" | 0' - 0 13/16" |
| 2L3-1/2X3X5/16SLBB | 3.91 in² | SLBB | 0' - 0" | 13.3 | 0' - 3 1/2" | 0' - 3" | 0' - 0 5/16" | 0' - 0 13/16" |
| 2L3-1/2X3X5/16X3/8SLBB | 3.91 in² | SLBB | 0' - 0 3/8" | 13.3 | 0' - 3 1/2" | 0' - 3" | 0' - 0 5/16" | 0' - 0 13/16" |
| 2L3-1/2X3X5/16X3/4SLBB | 3.91 in² | SLBB | 0' - 0 3/4" | 13.3 | 0' - 3 1/2" | 0' - 3" | 0' - 0 5/16" | 0' - 0 13/16" |
| 2L3-1/2X3X1/4SLBB | 3.16 in² | SLBB | 0' - 0" | 10.8 | 0' - 3 1/2" | 0' - 3" | 0' - 0 1/4" | 0' - 0 3/4" |
| 2L3-1/2X3X1/4X3/8SLBB | 3.16 in² | SLBB | 0' - 0 3/8" | 10.8 | 0' - 3 1/2" | 0' - 3" | 0' - 0 1/4" | 0' - 0 3/4" |
| 2L3-1/2X3X1/4X3/4SLBB | 3.16 in² | SLBB | 0' - 0 3/4" | 10.8 | 0' - 3 1/2" | 0' - 3" | 0' - 0 1/4" | 0' - 0 3/4" |
| 2L3-1/2X2-1/2X1/2SLBB | 5.53 in² | SLBB | 0' - 0" | 18.8 | 0' - 3 1/2" | 0' - 2 1/2" | 0' - 0 1/2" | 0' - 0 11/16" |
| 2L3-1/2X2-1/2X1/2X3/8SLBB | 5.53 in² | SLBB | 0' - 0 3/8" | 18.8 | 0' - 3 1/2" | 0' - 2 1/2" | 0' - 0 1/2" | 0' - 0 11/16" |
| 2L3-1/2X2-1/2X1/2X3/4SLBB | 5.53 in² | SLBB | 0' - 0 3/4" | 18.8 | 0' - 3 1/2" | 0' - 2 1/2" | 0' - 0 1/2" | 0' - 0 11/16" |
| 2L3-1/2X2-1/2X3/8SLBB | 4.25 in² | SLBB | 0' - 0" | 14.5 | 0' - 3 1/2" | 0' - 2 1/2" | 0' - 0 3/8" | 0' - 0 5/8" |
| 2L3-1/2X2-1/2X3/8X3/8SLBB | 4.25 in² | SLBB | 0' - 0 3/8" | 14.5 | 0' - 3 1/2" | 0' - 2 1/2" | 0' - 0 3/8" | 0' - 0 5/8" |
| 2L3-1/2X2-1/2X3/8X3/4SLBB | 4.25 in² | SLBB | 0' - 0 3/4" | 14.5 | 0' - 3 1/2" | 0' - 2 1/2" | 0' - 0 3/8" | 0' - 0 5/8" |
| 2L3-1/2X2-1/2X5/16SLBB | 3.58 in² | SLBB | 0' - 0" | 12.2 | 0' - 3 1/2" | 0' - 2 1/2" | 0' - 0 5/16" | 0' - 0 5/8" |
| 2L3-1/2X2-1/2X5/16X3/8SLBB | 3.58 in² | SLBB | 0' - 0 3/8" | 12.2 | 0' - 3 1/2" | 0' - 2 1/2" | 0' - 0 5/16" | 0' - 0 5/8" |
| 2L3-1/2X2-1/2X5/16X3/4SLBB | 3.58 in² | SLBB | 0' - 0 3/4" | 12.2 | 0' - 3 1/2" | 0' - 2 1/2" | 0' - 0 5/16" | 0' - 0 5/8" |
| 2L3-1/2X2-1/2X1/4SLBB | 2.9 in² | SLBB | 0' - 0" | 9.88 | 0' - 3 1/2" | 0' - 2 1/2" | 0' - 0 1/4" | 0' - 0 5/8" |
| 2L3-1/2X2-1/2X1/4X3/8SLBB | 2.9 in² | SLBB | 0' - 0 3/8" | 9.88 | 0' - 3 1/2" | 0' - 2 1/2" | 0' - 0 1/4" | 0' - 0 5/8" |
| 2L3-1/2X2-1/2X1/4X3/4SLBB | 2.9 in² | SLBB | 0' - 0 3/4" | 9.88 | 0' - 3 1/2" | 0' - 2 1/2" | 0' - 0 1/4" | 0' - 0 5/8" |
| 2L3X2-1/2X1/2SLBB | 5.01 in² | SLBB | 0' - 0" | 17.1 | 0' - 3" | 0' - 2 1/2" | 0' - 0 1/2" | 0' - 0 3/4" |
| 2L3X2-1/2X1/2X3/8SLBB | 5.01 in² | SLBB | 0' - 0 3/8" | 17.1 | 0' - 3" | 0' - 2 1/2" | 0' - 0 1/2" | 0' - 0 3/4" |
| 2L3X2-1/21/2X3/4SLBB | 5.01 in² | SLBB | 0' - 0 3/4" | 17.1 | 0' - 3" | 0' - 2 1/2" | 0' - 0 1/2" | 0' - 0 3/4" |
| 2L3X2-1/2X7/16SLBB | 4.44 in² | SLBB | 0' - 0" | 15.1 | 0' - 3" | 0' - 2 1/2" | 0' - 0 7/16" | 0' - 0 3/4" |
| 2L3X2-1/2X7/16X3/8SLBB | 4.44 in² | SLBB | 0' - 0 3/8" | 15.1 | 0' - 3" | 0' - 2 1/2" | 0' - 0 7/16" | 0' - 0 3/4" |
| 2L3X2-1/2X7/16X3/4SLBB | 4.44 in² | SLBB | 0' - 0 3/4" | 15.1 | 0' - 3" | 0' - 2 1/2" | 0' - 0 7/16" | 0' - 0 3/4" |
| 2L3X2-1/2X3/8SLBB | 3.86 in² | SLBB | 0' - 0" | 13.1 | 0' - 3" | 0' - 2 1/2" | 0' - 0 3/8" | 0' - 0 11/16" |
| 2L3X2-1/2X3/8X3/8SLBB | 3.86 in² | SLBB | 0' - 0 3/8" | 13.1 | 0' - 3" | 0' - 2 1/2" | 0' - 0 3/8" | 0' - 0 11/16" |
| 2L3X2-1/2X3/8X3/4SLBB | 3.86 in² | SLBB | 0' - 0 3/4" | 13.1 | 0' - 3" | 0' - 2 1/2" | 0' - 0 3/8" | 0' - 0 11/16" |
| 2L3X2-1/2X5/16SLBB | 3.25 in² | SLBB | 0' - 0" | 11.1 | 0' - 3" | 0' - 2 1/2" | 0' - 0 5/16" | 0' - 0 11/16" |
| 2L3X2-1/2X5/16X3/8SLBB | 3.25 in² | SLBB | 0' - 0 3/8" | 11.1 | 0' - 3" | 0' - 2 1/2" | 0' - 0 5/16" | 0' - 0 11/16" |
| 2L3X2-1/2X5/16X3/4SLBB | 3.25 in² | SLBB | 0' - 0 3/4" | 11.1 | 0' - 3" | 0' - 2 1/2" | 0' - 0 5/16" | 0' - 0 11/16" |
| 2L3X2-1/2X1/4SLBB | 2.64 in² | SLBB | 0' - 0" | 8.97 | 0' - 3" | 0' - 2 1/2" | 0' - 0 1/4" | 0' - 0 5/8" |
| 2L3X2-1/2X1/4X3/8SLBB | 2.64 in² | SLBB | 0' - 0 3/8" | 8.97 | 0' - 3" | 0' - 2 1/2" | 0' - 0 1/4" | 0' - 0 5/8" |
| 2L3X2-1/2X1/4X3/4SLBB | 2.64 in² | SLBB | 0' - 0 3/4" | 8.97 | 0' - 3" | 0' - 2 1/2" | 0' - 0 1/4" | 0' - 0 5/8" |
| 2L3X2-1/2X3/16SLBB | 2 in² | SLBB | 0' - 0" | 6.82 | 0' - 3" | 0' - 2 1/2" | 0' - 0 3/16" | 0' - 0 5/8" |
| 2L3X2-1/2X3/16X3/8SLBB | 2 in² | SLBB | 0' - 0 3/8" | 6.82 | 0' - 3" | 0' - 2 1/2" | 0' - 0 3/16" | 0' - 0 5/8" |
| 2L3X2-1/2X3/16X3/4SLBB | 2 in² | SLBB | 0' - 0 3/4" | 6.82 | 0' - 3" | 0' - 2 1/2" | 0' - 0 3/16" | 0' - 0 5/8" |
| 2L3X2X1/2SLBB | 4.53 in² | SLBB | 0' - 0" | 15.4 | 0' - 3" | 0' - 2" | 0' - 0 1/2" | 0' - 0 9/16" |
| 2L3X2X1/2X3/8SLBB | 4.53 in² | SLBB | 0' - 0 3/8" | 15.4 | 0' - 3" | 0' - 2" | 0' - 0 1/2" | 0' - 0 9/16" |
| 2L3X2X1/2X3/4SLBB | 4.53 in² | SLBB | 0' - 0 3/4" | 15.4 | 0' - 3" | 0' - 2" | 0' - 0 1/2" | 0' - 0 9/16" |
| 2L3X2X3/8SLBB | 3.5 in² | SLBB | 0' - 0" | 11.9 | 0' - 3" | 0' - 2" | 0' - 0 3/8" | 0' - 0 9/16" |
| 2L3X2X3/8X3/8SLBB | 3.5 in² | SLBB | 0' - 0 3/8" | 11.9 | 0' - 3" | 0' - 2" | 0' - 0 3/8" | 0' - 0 9/16" |
| 2L3X2X3/8X3/4SLBB | 3.5 in² | SLBB | 0' - 0 3/4" | 11.9 | 0' - 3" | 0' - 2" | 0' - 0 3/8" | 0' - 0 9/16" |
| 2L3X2X5/16SLBB | 2.96 in² | SLBB | 0' - 0" | 10.1 | 0' - 3" | 0' - 2" | 0' - 0 5/16" | 0' - 0 1/2" |
| 2L3X2X5/16X3/8SLBB | 2.96 in² | SLBB | 0' - 0 3/8" | 10.1 | 0' - 3" | 0' - 2" | 0' - 0 5/16" | 0' - 0 1/2" |
| 2L3X2X5/16X3/4SLBB | 2.96 in² | SLBB | 0' - 0 3/4" | 10.1 | 0' - 3" | 0' - 2" | 0' - 0 5/16" | 0' - 0 1/2" |
| 2L3X2X1/4SLBB | 2.4 in² | SLBB | 0' - 0" | 8.18 | 0' - 3" | 0' - 2" | 0' - 0 1/4" | 0' - 0 1/2" |
| 2L3X2X1/4X3/8SLBB | 2.4 in² | SLBB | 0' - 0 3/8" | 8.18 | 0' - 3" | 0' - 2" | 0' - 0 1/4" | 0' - 0 1/2" |
| 2L3X2X1/4X3/4SLBB | 2.4 in² | SLBB | 0' - 0 3/4" | 8.18 | 0' - 3" | 0' - 2" | 0' - 0 1/4" | 0' - 0 1/2" |
| 2L3X2X3/16SLBB | 1.83 in² | SLBB | 0' - 0" | 6.24 | 0' - 3" | 0' - 2" | 0' - 0 3/16" | 0' - 0 7/16" |
| 2L3X2X3/16X3/8SLBB | 1.83 in² | SLBB | 0' - 0 3/8" | 6.24 | 0' - 3" | 0' - 2" | 0' - 0 3/16" | 0' - 0 7/16" |
| 2L3X2X3/16X3/4SLBB | 1.83 in² | SLBB | 0' - 0 3/4" | 6.24 | 0' - 3" | 0' - 2" | 0' - 0 3/16" | 0' - 0 7/16" |
| 2L2-1/2X2X3/8SLBB | 3.11 in² | SLBB | 0' - 0" | 10.6 | 0' - 2 1/2" | 0' - 2" | 0' - 0 3/8" | 0' - 0 9/16" |
| 2L2-1/2X2X3/8X3/8SLBB | 3.11 in² | SLBB | 0' - 0 3/8" | 10.6 | 0' - 2 1/2" | 0' - 2" | 0' - 0 3/8" | 0' - 0 9/16" |
| 2L2-1/2X2X3/8X3/4SLBB | 3.11 in² | SLBB | 0' - 0 3/4" | 10.6 | 0' - 2 1/2" | 0' - 2" | 0' - 0 3/8" | 0' - 0 9/16" |
| 2L2-1/2X2X5/16SLBB | 2.64 in² | SLBB | 0' - 0" | 8.97 | 0' - 2 1/2" | 0' - 2" | 0' - 0 5/16" | 0' - 0 9/16" |
| 2L2-1/2X2X5/16X3/8SLBB | 2.64 in² | SLBB | 0' - 0 3/8" | 8.97 | 0' - 2 1/2" | 0' - 2" | 0' - 0 5/16" | 0' - 0 9/16" |
| 2L2-1/2X2X5/16X3/4SLBB | 2.64 in² | SLBB | 0' - 0 3/4" | 8.97 | 0' - 2 1/2" | 0' - 2" | 0' - 0 5/16" | 0' - 0 9/16" |
| 2L2-1/2X2X1/4SLBB | 2.14 in² | SLBB | 0' - 0" | 7.3 | 0' - 2 1/2" | 0' - 2" | 0' - 0 1/4" | 0' - 0 9/16" |
| 2L2-1/2X2X1/4X3/8SLBB | 2.14 in² | SLBB | 0' - 0 3/8" | 7.3 | 0' - 2 1/2" | 0' - 2" | 0' - 0 1/4" | 0' - 0 9/16" |
| 2L2-1/2X2X1/4X3/4SLBB | 2.14 in² | SLBB | 0' - 0 3/4" | 7.3 | 0' - 2 1/2" | 0' - 2" | 0' - 0 1/4" | 0' - 0 9/16" |
| 2L2-1/2X2X3/16SLBB | 1.64 in² | SLBB | 0' - 0" | 5.57 | 0' - 2 1/2" | 0' - 2" | 0' - 0 3/16" | 0' - 0 1/2" |
| 2L2-1/2X2X3/16X3/8SLBB | 1.64 in² | SLBB | 0' - 0 3/8" | 5.57 | 0' - 2 1/2" | 0' - 2" | 0' - 0 3/16" | 0' - 0 1/2" |
| 2L2-1/2X2X3/16X3/4SLBB | 1.64 in² | SLBB | 0' - 0 3/4" | 5.57 | 0' - 2 1/2" | 0' - 2" | 0' - 0 3/16" | 0' - 0 1/2" |

## geometry (parser evidence)
native form markers: Sweep x1
no freeform markers — native parametric forms only
